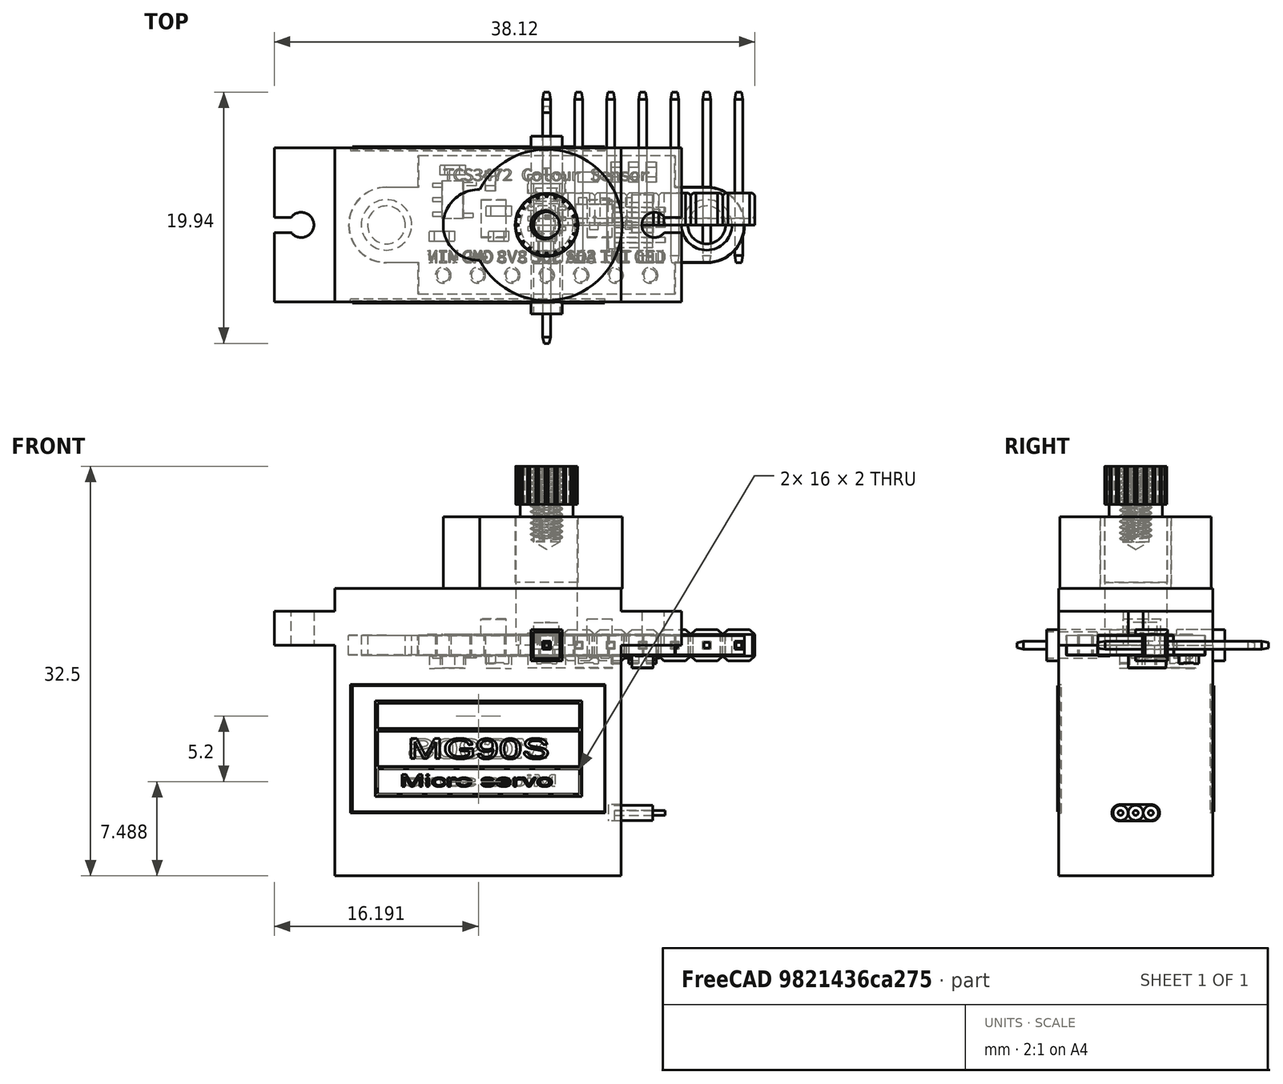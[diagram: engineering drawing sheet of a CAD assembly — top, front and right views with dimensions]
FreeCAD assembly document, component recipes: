
FREECAD ASSEMBLY — COMPONENT RECIPES ("Gems Sorter")

This assembly document has 104 components, labeled P0..P103 below (a component is one placed body or linked part). 33 of them carry a construction recipe — the FreeCAD feature program that regenerates the part from scratch, quoted from this document or its linked companion documents; the rest are supplied as boundary geometry only. No exploded tour is included for this assembly.
COMPONENT P0 — recipe-attached ("038_Base", modeled in this document).
Construction recipe (the document's own serialized feature program — sketch geometry with constraints, then the solid features built on it; lengths are millimeters unless a unit is written):

FEATURE [Sketcher::SketchObject] Sketch
  ArcFitTolerance = 1e-06
  AttachmentSupport = -> [XY_Plane]
  FullyConstrained = true
  MakeInternals = false
  MapMode = 5
  expr: Constraints[1] = VarSet.tube_inner_dia
  expr: Constraints[3] = VarSet.dowel_dia + 5 mm
  sketch-geometry (2):
    g0: Circle CenterX=0 CenterY=0 CenterZ=0 NormalX=0 NormalY=0 NormalZ=1 AngleXU=0 Radius=42.45
    g1: Circle CenterX=0 CenterY=0 CenterZ=0 NormalX=0 NormalY=0 NormalZ=1 AngleXU=0 Radius=31.25
  constraints (4):
    c: Coincident(g0,g-1)
    c: Diameter(g0) = 84.9
    c: Coincident(g1,g0)
    c: Distance(g1,g0) = 11.2
FEATURE [PartDesign::Pad] Pad
  Direction = (0,0,1)
  Length = 7.5
  Length2 = 10
  Profile = -> Sketch
  ReferenceAxis = -> Sketch [N_Axis]
  Refine = true
  Suppressed = false
  Type = 0
  expr: Length = VarSet.mdf_thickness
FEATURE [PartDesign::Plane] DatumPlane001
  AttachmentOffset = pos=(0,0,7.5) rot=(0,0,1;0rad)
  AttachmentSupport = -> [XY_Plane]
  Length = 101.88
  MapMode = 5
  Placement = pos=(0,0,7.5) rot=(0,0,1;0rad)
  ResizeMode = 0
  Width = 101.88
  expr: .AttachmentOffset.Base.z = VarSet.mdf_thickness
FEATURE [Sketcher::SketchObject] Sketch011
  ArcFitTolerance = 1e-06
  AttachmentSupport = -> [DatumPlane001]
  FullyConstrained = true
  MakeInternals = false
  MapMode = 5
  Placement = pos=(0,0,7.5) rot=(0,0,1;0rad)
  expr: Constraints[17] = VarSet.tube_inner_dia / 2 - 2.5 mm - VarSet.dowel_dia / 2
  expr: Constraints[1] = VarSet.dowel_dia
  expr: Constraints[2] = VarSet.tube_inner_dia / 2 - 2.5 mm - VarSet.dowel_dia / 2
  expr: Constraints[6] = VarSet.tube_inner_dia / 2 - 2.5 mm - VarSet.dowel_dia / 2
  sketch-geometry (8):
    g0: Circle [constr] CenterX=-36.85 CenterY=0 CenterZ=0 NormalX=0 NormalY=0 NormalZ=1 AngleXU=0 Radius=3.1
    g1: Circle CenterX=-31.913 CenterY=18.425 CenterZ=0 NormalX=0 NormalY=0 NormalZ=1 AngleXU=0 Radius=3.1
    g2: Circle CenterX=-31.913 CenterY=-18.425 CenterZ=0 NormalX=0 NormalY=0 NormalZ=1 AngleXU=0 Radius=3.1
    g3: LineSegment [constr] StartX=-31.913 StartY=-18.425 StartZ=0 EndX=0 EndY=0 EndZ=0
    g4: Circle CenterX=-18.425 CenterY=31.913 CenterZ=0 NormalX=0 NormalY=0 NormalZ=1 AngleXU=0 Radius=3.1
    g5: Circle CenterX=-18.425 CenterY=-31.913 CenterZ=0 NormalX=0 NormalY=0 NormalZ=1 AngleXU=0 Radius=3.1
    g6: LineSegment [constr] StartX=-18.425 StartY=31.913 StartZ=0 EndX=0 EndY=-3.6e-15 EndZ=0
    g7: LineSegment [constr] StartX=0 StartY=0 StartZ=0 EndX=-18.425 EndY=-31.913 EndZ=0
  constraints (19):
    c: PointOnObject(g0,g-1)
    c: Diameter(g0) = 6.2
    c: Distance(g0,g-2) = 36.85
    c: Equal(g1,g2)
    c: Equal(g2,g0)
    c: Symmetric(g2,g1,g-1)
    c: Distance(g1,g-1) = 36.85
    c: Coincident(g3,g2)
    c: Coincident(g3,g-1)
    c: Angle(g-1,g3) = 0.523599
    c: Equal(g5,g4)
    c: Equal(g4,g2)
    c: Symmetric(g5,g4,g-1)
    c: Coincident(g6,g4)
    c: Coincident(g6,g3)
    c: Coincident(g7,g3)
    c: Coincident(g7,g5)
    c: Distance(g6,g6) = 36.85
    c: Angle(g6,g-1) = 1.0472
FEATURE [PartDesign::Pocket] Pocket003
  BaseFeature = -> Pad
  Direction = (0,0,-1)
  Length = 5
  Length2 = 5
  Profile = -> Sketch011
  ReferenceAxis = -> Sketch011 [N_Axis]
  Refine = true
  Suppressed = false
  Type = 1
FEATURE [PartDesign::Plane] DatumPlane004
  AttachmentOffset = pos=(0,0,42.45) rot=(0,0,1;0rad)
  AttachmentSupport = -> [XZ_Plane]
  Length = 97.9307
  MapMode = 5
  Placement = pos=(0,-42.45,9.4e-15) rot=(1,0,0;1.5708rad)
  ResizeMode = 0
  Width = 63.0307
  expr: .AttachmentOffset.Base.z = VarSet.tube_inner_dia / 2
FEATURE [Sketcher::SketchObject] Sketch024
  ArcFitTolerance = 1e-06
  AttachmentSupport = -> [DatumPlane004]
  FullyConstrained = true
  MakeInternals = false
  MapMode = 5
  Placement = pos=(0,-42.45,9.4e-15) rot=(1,0,0;1.5708rad)
  expr: Constraints[2] = VarSet.mdf_thickness / 2
  sketch-geometry (1):
    g0: Circle CenterX=0 CenterY=3.75 CenterZ=0 NormalX=0 NormalY=0 NormalZ=1 AngleXU=0 Radius=1
  constraints (3):
    c: Diameter(g0) = 2
    c: PointOnObject(g0,g-2)
    c: Distance(g0,g-1) = 3.75
FEATURE [PartDesign::Pocket] Pocket012
  BaseFeature = -> Pocket003
  Direction = (0,1,-2e-16)
  Length = 6
  Length2 = 5
  Profile = -> Sketch024
  ReferenceAxis = -> Sketch024 [N_Axis]
  Refine = true
  Suppressed = false
  Type = 0
FEATURE [PartDesign::PolarPattern] PolarPattern001
  Angle = 180
  Axis = -> Z_Axis
  BaseFeature = -> Pocket012
  Mode = 0
  Occurrences = 3
  Offset = 120
  Originals = -> [Pocket012]
  Refine = true
  Reversed = true
  Suppressed = false
  TransformMode = 0
FEATURE [PartDesign::Body] Body  label="ring_spacer"
  AllowCompound = false
  Group = -> [Sketch,Pad,DatumPlane001,Sketch011,Pocket003,DatumPlane004,Sketch024,Pocket012,PolarPattern001]
  Origin = -> Origin
  Placement = pos=(0,0,-12) rot=(0,0,1;0rad)
  Tip = -> PolarPattern001
COMPONENT P1 — same part as P0; its construction recipe is shown at P0.
COMPONENT P2 — same part as P0; its construction recipe is shown at P0.
COMPONENT P3 — geometry summary ("059_BreadBoard001"; no construction recipe available for this part):
  bounding box: 83.8 x 55.5 x 8.0 mm
  tessellated surface: 18,878 triangles
  volume: 30349 mm^3 (81% of its bounding box)
COMPONENT P4 — recipe-attached ("037_Cap", modeled in this document).
Construction recipe (the document's own serialized feature program — sketch geometry with constraints, then the solid features built on it; lengths are millimeters unless a unit is written):

FEATURE [Sketcher::SketchObject] Sketch001
  ArcFitTolerance = 1e-06
  AttachmentSupport = -> [XY_Plane001]
  FullyConstrained = true
  MakeInternals = false
  MapMode = 5
  expr: Constraints[2] = VarSet.pipe_OD
  expr: Constraints[3] = VarSet.Pipe_thickness
  sketch-geometry (2):
    g0: Circle CenterX=0 CenterY=0 CenterZ=0 NormalX=0 NormalY=0 NormalZ=1 AngleXU=0 Radius=45
    g1: Circle CenterX=0 CenterY=0 CenterZ=0 NormalX=0 NormalY=0 NormalZ=1 AngleXU=0 Radius=40
  constraints (4):
    c: Coincident(g0,g-1)
    c: Coincident(g1,g0)
    c: Diameter(g0) = 90
    c: Distance(g1,g0) = 5
FEATURE [PartDesign::Pad] Pad001
  Direction = (0,0,1)
  Length = 50
  Length2 = 10
  Profile = -> Sketch001
  ReferenceAxis = -> Sketch001 [N_Axis]
  Refine = true
  Suppressed = false
  Type = 0
FEATURE [PartDesign::Body] Body001  label="Pipe"
  AllowCompound = false
  Group = -> [Sketch001,Pad001]
  Origin = -> Origin001
  Placement = pos=(0,0,-42) rot=(0,0,1;0rad)
  Tip = -> Pad001
COMPONENT P5 — geometry summary ("032_Cut"; no construction recipe available for this part):
  bounding box: 32.7 x 16.0 x 9.6 mm
  tessellated surface: 1,810 triangles
  volume: 2244 mm^3 (45% of its bounding box)
COMPONENT P6 — geometry summary ("016_M90S_ali001"; no construction recipe available for this part):
  bounding box: 32.5 x 32.3 x 12.4 mm
  tessellated surface: 12,672 triangles
  volume: 7441 mm^3 (57% of its bounding box)
  symmetry: mirror-symmetric across its x mid-plane
COMPONENT P7 — geometry summary ("029_M90S_ali002"; no construction recipe available for this part):
  bounding box: 32.5 x 32.3 x 12.4 mm
  tessellated surface: 12,672 triangles
  volume: 7441 mm^3 (57% of its bounding box)
  symmetry: mirror-symmetric across its x mid-plane
COMPONENT P8 — geometry summary ("061_Pin001"; no construction recipe available for this part):
  bounding box: 18.8 x 0.6 x 0.6 mm
  tessellated surface: 28 triangles
  volume: 8 mm^3 (98% of its bounding box)
  symmetry: 2-fold rotationally symmetric about the x axis; 2-fold rotationally symmetric about the y axis; 4-fold rotationally symmetric about the z axis; mirror-symmetric across its x mid-plane, y mid-plane, z mid-plane
COMPONENT P9 — geometry summary ("064_Pin002"; no construction recipe available for this part):
  bounding box: 18.8 x 0.6 x 0.6 mm
  tessellated surface: 28 triangles
  volume: 8 mm^3 (98% of its bounding box)
  symmetry: 2-fold rotationally symmetric about the x axis; 2-fold rotationally symmetric about the y axis; 4-fold rotationally symmetric about the z axis; mirror-symmetric across its x mid-plane, y mid-plane, z mid-plane
COMPONENT P10 — geometry summary ("066_Pin003"; no construction recipe available for this part):
  bounding box: 18.8 x 0.6 x 0.6 mm
  tessellated surface: 28 triangles
  volume: 8 mm^3 (98% of its bounding box)
  symmetry: 2-fold rotationally symmetric about the x axis; 2-fold rotationally symmetric about the y axis; 4-fold rotationally symmetric about the z axis; mirror-symmetric across its x mid-plane, y mid-plane, z mid-plane
COMPONENT P11 — geometry summary ("068_Pin004"; no construction recipe available for this part):
  bounding box: 18.8 x 0.6 x 0.6 mm
  tessellated surface: 28 triangles
  volume: 8 mm^3 (98% of its bounding box)
  symmetry: 2-fold rotationally symmetric about the x axis; 2-fold rotationally symmetric about the y axis; 4-fold rotationally symmetric about the z axis; mirror-symmetric across its x mid-plane, y mid-plane, z mid-plane
COMPONENT P12 — geometry summary ("069_Pin005"; no construction recipe available for this part):
  bounding box: 18.8 x 0.6 x 0.6 mm
  tessellated surface: 28 triangles
  volume: 8 mm^3 (98% of its bounding box)
  symmetry: 2-fold rotationally symmetric about the x axis; 2-fold rotationally symmetric about the y axis; 4-fold rotationally symmetric about the z axis; mirror-symmetric across its x mid-plane, y mid-plane, z mid-plane
COMPONENT P13 — geometry summary ("071_Pin006"; no construction recipe available for this part):
  bounding box: 18.8 x 0.6 x 0.6 mm
  tessellated surface: 28 triangles
  volume: 8 mm^3 (98% of its bounding box)
  symmetry: 2-fold rotationally symmetric about the x axis; 2-fold rotationally symmetric about the y axis; 4-fold rotationally symmetric about the z axis; mirror-symmetric across its x mid-plane, y mid-plane, z mid-plane
COMPONENT P14 — geometry summary ("073_Pin007"; no construction recipe available for this part):
  bounding box: 18.8 x 0.6 x 0.6 mm
  tessellated surface: 28 triangles
  volume: 8 mm^3 (98% of its bounding box)
  symmetry: 2-fold rotationally symmetric about the x axis; 2-fold rotationally symmetric about the y axis; 4-fold rotationally symmetric about the z axis; mirror-symmetric across its x mid-plane, y mid-plane, z mid-plane
COMPONENT P15 — geometry summary ("075_Pin008"; no construction recipe available for this part):
  bounding box: 18.8 x 0.6 x 0.6 mm
  tessellated surface: 28 triangles
  volume: 8 mm^3 (98% of its bounding box)
  symmetry: 2-fold rotationally symmetric about the x axis; 2-fold rotationally symmetric about the y axis; 4-fold rotationally symmetric about the z axis; mirror-symmetric across its x mid-plane, y mid-plane, z mid-plane
COMPONENT P16 — geometry summary ("077_Pin009"; no construction recipe available for this part):
  bounding box: 18.8 x 0.6 x 0.6 mm
  tessellated surface: 28 triangles
  volume: 8 mm^3 (98% of its bounding box)
  symmetry: 2-fold rotationally symmetric about the x axis; 2-fold rotationally symmetric about the y axis; 4-fold rotationally symmetric about the z axis; mirror-symmetric across its x mid-plane, y mid-plane, z mid-plane
COMPONENT P17 — geometry summary ("079_Pin010"; no construction recipe available for this part):
  bounding box: 18.8 x 0.6 x 0.6 mm
  tessellated surface: 28 triangles
  volume: 8 mm^3 (98% of its bounding box)
  symmetry: 2-fold rotationally symmetric about the x axis; 2-fold rotationally symmetric about the y axis; 4-fold rotationally symmetric about the z axis; mirror-symmetric across its x mid-plane, y mid-plane, z mid-plane
COMPONENT P18 — geometry summary ("081_Pin011"; no construction recipe available for this part):
  bounding box: 18.8 x 0.6 x 0.6 mm
  tessellated surface: 28 triangles
  volume: 8 mm^3 (98% of its bounding box)
  symmetry: 2-fold rotationally symmetric about the x axis; 2-fold rotationally symmetric about the y axis; 4-fold rotationally symmetric about the z axis; mirror-symmetric across its x mid-plane, y mid-plane, z mid-plane
COMPONENT P19 — geometry summary ("083_Pin012"; no construction recipe available for this part):
  bounding box: 18.8 x 0.6 x 0.6 mm
  tessellated surface: 28 triangles
  volume: 8 mm^3 (98% of its bounding box)
  symmetry: 2-fold rotationally symmetric about the x axis; 2-fold rotationally symmetric about the y axis; 4-fold rotationally symmetric about the z axis; mirror-symmetric across its x mid-plane, y mid-plane, z mid-plane
COMPONENT P20 — geometry summary ("085_Pin013"; no construction recipe available for this part):
  bounding box: 18.8 x 0.6 x 0.6 mm
  tessellated surface: 28 triangles
  volume: 8 mm^3 (98% of its bounding box)
  symmetry: 2-fold rotationally symmetric about the x axis; 2-fold rotationally symmetric about the y axis; 4-fold rotationally symmetric about the z axis; mirror-symmetric across its x mid-plane, y mid-plane, z mid-plane
COMPONENT P21 — geometry summary ("087_Pin014"; no construction recipe available for this part):
  bounding box: 18.8 x 0.6 x 0.6 mm
  tessellated surface: 28 triangles
  volume: 8 mm^3 (98% of its bounding box)
  symmetry: 2-fold rotationally symmetric about the x axis; 2-fold rotationally symmetric about the y axis; 4-fold rotationally symmetric about the z axis; mirror-symmetric across its x mid-plane, y mid-plane, z mid-plane
COMPONENT P22 — geometry summary ("089_Pin015"; no construction recipe available for this part):
  bounding box: 18.8 x 0.6 x 0.6 mm
  tessellated surface: 28 triangles
  volume: 8 mm^3 (98% of its bounding box)
  symmetry: 2-fold rotationally symmetric about the x axis; 2-fold rotationally symmetric about the y axis; 4-fold rotationally symmetric about the z axis; mirror-symmetric across its x mid-plane, y mid-plane, z mid-plane
COMPONENT P23 — geometry summary ("091_Pin016"; no construction recipe available for this part):
  bounding box: 18.8 x 0.6 x 0.6 mm
  tessellated surface: 28 triangles
  volume: 8 mm^3 (98% of its bounding box)
  symmetry: 2-fold rotationally symmetric about the x axis; 2-fold rotationally symmetric about the y axis; 4-fold rotationally symmetric about the z axis; mirror-symmetric across its x mid-plane, y mid-plane, z mid-plane
COMPONENT P24 — geometry summary ("093_Pin017"; no construction recipe available for this part):
  bounding box: 18.8 x 0.6 x 0.6 mm
  tessellated surface: 28 triangles
  volume: 8 mm^3 (98% of its bounding box)
  symmetry: 2-fold rotationally symmetric about the x axis; 2-fold rotationally symmetric about the y axis; 4-fold rotationally symmetric about the z axis; mirror-symmetric across its x mid-plane, y mid-plane, z mid-plane
COMPONENT P25 — geometry summary ("095_Pin018"; no construction recipe available for this part):
  bounding box: 18.8 x 0.6 x 0.6 mm
  tessellated surface: 28 triangles
  volume: 8 mm^3 (98% of its bounding box)
  symmetry: 2-fold rotationally symmetric about the x axis; 2-fold rotationally symmetric about the y axis; 4-fold rotationally symmetric about the z axis; mirror-symmetric across its x mid-plane, y mid-plane, z mid-plane
COMPONENT P26 — geometry summary ("097_Pin019"; no construction recipe available for this part):
  bounding box: 18.8 x 0.6 x 0.6 mm
  tessellated surface: 28 triangles
  volume: 8 mm^3 (98% of its bounding box)
  symmetry: 2-fold rotationally symmetric about the x axis; 2-fold rotationally symmetric about the y axis; 4-fold rotationally symmetric about the z axis; mirror-symmetric across its x mid-plane, y mid-plane, z mid-plane
COMPONENT P27 — geometry summary ("099_Pin020"; no construction recipe available for this part):
  bounding box: 18.8 x 0.6 x 0.6 mm
  tessellated surface: 28 triangles
  volume: 8 mm^3 (98% of its bounding box)
  symmetry: 2-fold rotationally symmetric about the x axis; 2-fold rotationally symmetric about the y axis; 4-fold rotationally symmetric about the z axis; mirror-symmetric across its x mid-plane, y mid-plane, z mid-plane
COMPONENT P28 — geometry summary ("050_Socket001"; no construction recipe available for this part):
  bounding box: 14.1 x 2.5 x 2.5 mm
  tessellated surface: 220 triangles
  volume: 52 mm^3 (59% of its bounding box)
  symmetry: mirror-symmetric across its y mid-plane
COMPONENT P29 — geometry summary ("051_Socket002"; no construction recipe available for this part):
  bounding box: 14.1 x 2.5 x 2.5 mm
  tessellated surface: 220 triangles
  volume: 52 mm^3 (59% of its bounding box)
  symmetry: mirror-symmetric across its y mid-plane
COMPONENT P30 — geometry summary ("052_Socket003"; no construction recipe available for this part):
  bounding box: 14.1 x 2.5 x 2.5 mm
  tessellated surface: 220 triangles
  volume: 52 mm^3 (59% of its bounding box)
  symmetry: mirror-symmetric across its y mid-plane
COMPONENT P31 — geometry summary ("056_Socket004"; no construction recipe available for this part):
  bounding box: 14.1 x 2.5 x 2.5 mm
  tessellated surface: 220 triangles
  volume: 52 mm^3 (59% of its bounding box)
  symmetry: mirror-symmetric across its y mid-plane
COMPONENT P32 — geometry summary ("057_Socket005"; no construction recipe available for this part):
  bounding box: 14.1 x 2.5 x 2.5 mm
  tessellated surface: 220 triangles
  volume: 52 mm^3 (59% of its bounding box)
  symmetry: mirror-symmetric across its y mid-plane
COMPONENT P33 — geometry summary ("058_Socket006"; no construction recipe available for this part):
  bounding box: 14.1 x 2.5 x 2.5 mm
  tessellated surface: 220 triangles
  volume: 52 mm^3 (59% of its bounding box)
  symmetry: mirror-symmetric across its y mid-plane
COMPONENT P34 — geometry summary ("062_Socket007"; no construction recipe available for this part):
  bounding box: 14.1 x 2.5 x 2.5 mm
  tessellated surface: 220 triangles
  volume: 52 mm^3 (59% of its bounding box)
  symmetry: mirror-symmetric across its y mid-plane
COMPONENT P35 — geometry summary ("063_Socket008"; no construction recipe available for this part):
  bounding box: 14.1 x 2.5 x 2.5 mm
  tessellated surface: 220 triangles
  volume: 52 mm^3 (59% of its bounding box)
  symmetry: mirror-symmetric across its y mid-plane
COMPONENT P36 — geometry summary ("065_Socket009"; no construction recipe available for this part):
  bounding box: 14.1 x 2.5 x 2.5 mm
  tessellated surface: 220 triangles
  volume: 52 mm^3 (59% of its bounding box)
  symmetry: mirror-symmetric across its y mid-plane
COMPONENT P37 — geometry summary ("067_Socket010"; no construction recipe available for this part):
  bounding box: 14.1 x 2.5 x 2.5 mm
  tessellated surface: 220 triangles
  volume: 52 mm^3 (59% of its bounding box)
  symmetry: mirror-symmetric across its y mid-plane
COMPONENT P38 — geometry summary ("070_Socket011"; no construction recipe available for this part):
  bounding box: 14.1 x 2.5 x 2.5 mm
  tessellated surface: 220 triangles
  volume: 52 mm^3 (59% of its bounding box)
  symmetry: mirror-symmetric across its y mid-plane
COMPONENT P39 — geometry summary ("072_Socket012"; no construction recipe available for this part):
  bounding box: 14.1 x 2.5 x 2.5 mm
  tessellated surface: 220 triangles
  volume: 52 mm^3 (59% of its bounding box)
  symmetry: mirror-symmetric across its y mid-plane
COMPONENT P40 — geometry summary ("074_Socket013"; no construction recipe available for this part):
  bounding box: 14.1 x 2.5 x 2.5 mm
  tessellated surface: 220 triangles
  volume: 52 mm^3 (59% of its bounding box)
  symmetry: mirror-symmetric across its y mid-plane
COMPONENT P41 — geometry summary ("076_Socket014"; no construction recipe available for this part):
  bounding box: 14.1 x 2.5 x 2.5 mm
  tessellated surface: 220 triangles
  volume: 52 mm^3 (59% of its bounding box)
  symmetry: mirror-symmetric across its y mid-plane
COMPONENT P42 — geometry summary ("078_Socket015"; no construction recipe available for this part):
  bounding box: 14.1 x 2.5 x 2.5 mm
  tessellated surface: 220 triangles
  volume: 52 mm^3 (59% of its bounding box)
  symmetry: mirror-symmetric across its y mid-plane
COMPONENT P43 — geometry summary ("080_Socket016"; no construction recipe available for this part):
  bounding box: 14.1 x 2.5 x 2.5 mm
  tessellated surface: 220 triangles
  volume: 52 mm^3 (59% of its bounding box)
  symmetry: mirror-symmetric across its y mid-plane
COMPONENT P44 — geometry summary ("082_Socket017"; no construction recipe available for this part):
  bounding box: 14.1 x 2.5 x 2.5 mm
  tessellated surface: 220 triangles
  volume: 52 mm^3 (59% of its bounding box)
  symmetry: mirror-symmetric across its y mid-plane
COMPONENT P45 — geometry summary ("084_Socket018"; no construction recipe available for this part):
  bounding box: 14.1 x 2.5 x 2.5 mm
  tessellated surface: 220 triangles
  volume: 52 mm^3 (59% of its bounding box)
  symmetry: mirror-symmetric across its y mid-plane
COMPONENT P46 — geometry summary ("086_Socket019"; no construction recipe available for this part):
  bounding box: 14.1 x 2.5 x 2.5 mm
  tessellated surface: 220 triangles
  volume: 52 mm^3 (59% of its bounding box)
  symmetry: mirror-symmetric across its y mid-plane
COMPONENT P47 — geometry summary ("088_Socket020"; no construction recipe available for this part):
  bounding box: 14.1 x 2.5 x 2.5 mm
  tessellated surface: 220 triangles
  volume: 52 mm^3 (59% of its bounding box)
  symmetry: mirror-symmetric across its y mid-plane
COMPONENT P48 — geometry summary ("090_Socket021"; no construction recipe available for this part):
  bounding box: 14.1 x 2.5 x 2.5 mm
  tessellated surface: 220 triangles
  volume: 52 mm^3 (59% of its bounding box)
  symmetry: mirror-symmetric across its y mid-plane
COMPONENT P49 — geometry summary ("092_Socket022"; no construction recipe available for this part):
  bounding box: 14.1 x 2.5 x 2.5 mm
  tessellated surface: 220 triangles
  volume: 52 mm^3 (59% of its bounding box)
  symmetry: mirror-symmetric across its y mid-plane
COMPONENT P50 — geometry summary ("094_Socket023"; no construction recipe available for this part):
  bounding box: 14.1 x 2.5 x 2.5 mm
  tessellated surface: 220 triangles
  volume: 52 mm^3 (59% of its bounding box)
  symmetry: mirror-symmetric across its y mid-plane
COMPONENT P51 — geometry summary ("096_Socket024"; no construction recipe available for this part):
  bounding box: 14.1 x 2.5 x 2.5 mm
  tessellated surface: 220 triangles
  volume: 52 mm^3 (59% of its bounding box)
  symmetry: mirror-symmetric across its y mid-plane
COMPONENT P52 — geometry summary ("098_Socket025"; no construction recipe available for this part):
  bounding box: 14.1 x 2.5 x 2.5 mm
  tessellated surface: 220 triangles
  volume: 52 mm^3 (59% of its bounding box)
  symmetry: mirror-symmetric across its y mid-plane
COMPONENT P53 — geometry summary ("100_Socket026"; no construction recipe available for this part):
  bounding box: 14.1 x 2.5 x 2.5 mm
  tessellated surface: 220 triangles
  volume: 52 mm^3 (59% of its bounding box)
  symmetry: mirror-symmetric across its y mid-plane
COMPONENT P54 — geometry summary ("101_Socket027"; no construction recipe available for this part):
  bounding box: 14.1 x 2.5 x 2.5 mm
  tessellated surface: 220 triangles
  volume: 52 mm^3 (59% of its bounding box)
  symmetry: mirror-symmetric across its y mid-plane
COMPONENT P55 — geometry summary ("102_Socket028"; no construction recipe available for this part):
  bounding box: 14.1 x 2.5 x 2.5 mm
  tessellated surface: 220 triangles
  volume: 52 mm^3 (59% of its bounding box)
  symmetry: mirror-symmetric across its y mid-plane
COMPONENT P56 — geometry summary ("103_Socket029"; no construction recipe available for this part):
  bounding box: 14.1 x 2.5 x 2.5 mm
  tessellated surface: 220 triangles
  volume: 52 mm^3 (59% of its bounding box)
  symmetry: mirror-symmetric across its y mid-plane
COMPONENT P57 — geometry summary ("104_Socket030"; no construction recipe available for this part):
  bounding box: 14.1 x 2.5 x 2.5 mm
  tessellated surface: 220 triangles
  volume: 52 mm^3 (59% of its bounding box)
  symmetry: mirror-symmetric across its y mid-plane
COMPONENT P58 — geometry summary ("020_#2x1/4in-Screw001"; no construction recipe available for this part):
  bounding box: 6.3 x 4.1 x 4.1 mm
  tessellated surface: 3,434 triangles
  volume: 23 mm^3 (22% of its bounding box)
  symmetry: 4-fold rotationally symmetric about the z axis; mirror-symmetric across its y mid-plane
COMPONENT P59 — geometry summary ("021_#2x1/4in-Screw002"; no construction recipe available for this part):
  bounding box: 6.3 x 4.1 x 4.1 mm
  tessellated surface: 3,434 triangles
  volume: 23 mm^3 (22% of its bounding box)
  symmetry: 4-fold rotationally symmetric about the z axis; mirror-symmetric across its y mid-plane
COMPONENT P60 — geometry summary ("030_#2x1/4in-Screw003"; no construction recipe available for this part):
  bounding box: 6.3 x 4.1 x 4.1 mm
  tessellated surface: 3,434 triangles
  volume: 23 mm^3 (22% of its bounding box)
  symmetry: 4-fold rotationally symmetric about the z axis; mirror-symmetric across its y mid-plane
COMPONENT P61 — geometry summary ("031_#2x1/4in-Screw004"; no construction recipe available for this part):
  bounding box: 6.3 x 4.1 x 4.1 mm
  tessellated surface: 3,434 triangles
  volume: 23 mm^3 (22% of its bounding box)
  symmetry: 4-fold rotationally symmetric about the z axis; mirror-symmetric across its y mid-plane
COMPONENT P62 — geometry summary ("003_#3x3/8in-Screw001"; no construction recipe available for this part):
  bounding box: 9.5 x 4.5 x 4.5 mm
  tessellated surface: 2,432 triangles
  volume: 52 mm^3 (27% of its bounding box)
  symmetry: 2-fold rotationally symmetric about the y axis; mirror-symmetric across its x mid-plane, z mid-plane
COMPONENT P63 — geometry summary ("004_#3x3/8in-Screw002"; no construction recipe available for this part):
  bounding box: 9.5 x 4.5 x 4.5 mm
  tessellated surface: 2,432 triangles
  volume: 52 mm^3 (27% of its bounding box)
  symmetry: 2-fold rotationally symmetric about the y axis; mirror-symmetric across its x mid-plane, z mid-plane
COMPONENT P64 — geometry summary ("005_#3x3/8in-Screw003"; no construction recipe available for this part):
  bounding box: 9.5 x 4.5 x 4.5 mm
  tessellated surface: 2,432 triangles
  volume: 52 mm^3 (27% of its bounding box)
  symmetry: 2-fold rotationally symmetric about the y axis; mirror-symmetric across its x mid-plane, z mid-plane
COMPONENT P65 — geometry summary ("010_#3x3/8in-Screw004"; no construction recipe available for this part):
  bounding box: 9.5 x 4.5 x 4.5 mm
  tessellated surface: 2,432 triangles
  volume: 52 mm^3 (27% of its bounding box)
  symmetry: 2-fold rotationally symmetric about the y axis; mirror-symmetric across its x mid-plane, z mid-plane
COMPONENT P66 — geometry summary ("011_#3x3/8in-Screw005"; no construction recipe available for this part):
  bounding box: 9.5 x 4.5 x 4.5 mm
  tessellated surface: 2,432 triangles
  volume: 52 mm^3 (27% of its bounding box)
  symmetry: 2-fold rotationally symmetric about the y axis; mirror-symmetric across its x mid-plane, z mid-plane
COMPONENT P67 — geometry summary ("012_#3x3/8in-Screw006"; no construction recipe available for this part):
  bounding box: 9.5 x 4.5 x 4.5 mm
  tessellated surface: 2,432 triangles
  volume: 52 mm^3 (27% of its bounding box)
  symmetry: 2-fold rotationally symmetric about the y axis; mirror-symmetric across its x mid-plane, z mid-plane
COMPONENT P68 — geometry summary ("013_#3x3/8in-Screw007"; no construction recipe available for this part):
  bounding box: 9.5 x 4.5 x 4.5 mm
  tessellated surface: 2,432 triangles
  volume: 52 mm^3 (27% of its bounding box)
  symmetry: 2-fold rotationally symmetric about the y axis; mirror-symmetric across its x mid-plane, z mid-plane
COMPONENT P69 — geometry summary ("018_#3x3/8in-Screw008"; no construction recipe available for this part):
  bounding box: 9.5 x 4.5 x 4.5 mm
  tessellated surface: 2,432 triangles
  volume: 52 mm^3 (27% of its bounding box)
  symmetry: 2-fold rotationally symmetric about the y axis; mirror-symmetric across its x mid-plane, z mid-plane
COMPONENT P70 — geometry summary ("019_#3x3/8in-Screw009"; no construction recipe available for this part):
  bounding box: 9.5 x 4.5 x 4.5 mm
  tessellated surface: 2,432 triangles
  volume: 52 mm^3 (27% of its bounding box)
  symmetry: 2-fold rotationally symmetric about the y axis; mirror-symmetric across its x mid-plane, z mid-plane
COMPONENT P71 — geometry summary ("060_+++ ESP8266 NodeMCU Board +++001"; no construction recipe available for this part):
  bounding box: 48.5 x 25.7 x 12.4 mm
  tessellated surface: 45,128 triangles
  volume: 3253 mm^3 (21% of its bounding box)
COMPONENT P72 — recipe-attached ("034_3m-foam001", modeled in this document).
Construction recipe (the document's own serialized feature program — sketch geometry with constraints, then the solid features built on it; lengths are millimeters unless a unit is written):

FEATURE [Sketcher::SketchObject] Sketch027
  ArcFitTolerance = 1e-06
  AttachmentSupport = -> [XY_Plane018]
  FullyConstrained = true
  MakeInternals = false
  MapMode = 5
  sketch-geometry (5):
    g0: LineSegment StartX=-5 StartY=-7.5 StartZ=0 EndX=5 EndY=-7.5 EndZ=0
    g1: LineSegment StartX=5 StartY=-7.5 StartZ=0 EndX=5 EndY=7.5 EndZ=0
    g2: LineSegment StartX=5 StartY=7.5 StartZ=0 EndX=-5 EndY=7.5 EndZ=0
    g3: LineSegment StartX=-5 StartY=7.5 StartZ=0 EndX=-5 EndY=-7.5 EndZ=0
    g4: GeomPoint [constr] X=0 Y=0 Z=0
  constraints (12):
    c: Coincident(g0,g1)
    c: Coincident(g1,g2)
    c: Coincident(g2,g3)
    c: Coincident(g3,g0)
    c: Horizontal(g0)
    c: Horizontal(g2)
    c: Vertical(g1)
    c: Vertical(g3)
    c: Symmetric(g2,g0,g4)
    c: Distance(g1,g3) = 10
    c: Distance(g0,g2) = 15
    c: Coincident(g4,g-1)
FEATURE [PartDesign::Pad] Pad011
  Direction = (0,0,1)
  Length = 1
  Length2 = 10
  Profile = -> Sketch027
  ReferenceAxis = -> Sketch027 [N_Axis]
  Refine = true
  Suppressed = false
  Type = 0
FEATURE [PartDesign::Body] Body012  label="3m-foam"
  AllowCompound = false
  Group = -> [Sketch027,Pad011]
  Origin = -> Origin018
  Tip = -> Pad011
COMPONENT P73 — same part as P72; its construction recipe is shown at P72.
COMPONENT P74 — recipe-attached ("033_3m-sticker001", modeled in this document).
Construction recipe (the document's own serialized feature program — sketch geometry with constraints, then the solid features built on it; lengths are millimeters unless a unit is written):

FEATURE [Sketcher::SketchObject] Sketch028
  ArcFitTolerance = 1e-06
  AttachmentSupport = -> [XY_Plane019]
  FullyConstrained = true
  MakeInternals = false
  MapMode = 5
  sketch-geometry (5):
    g0: LineSegment StartX=-5 StartY=-7.5 StartZ=0 EndX=5 EndY=-7.5 EndZ=0
    g1: LineSegment StartX=5 StartY=-7.5 StartZ=0 EndX=5 EndY=7.5 EndZ=0
    g2: LineSegment StartX=5 StartY=7.5 StartZ=0 EndX=-5 EndY=7.5 EndZ=0
    g3: LineSegment StartX=-5 StartY=7.5 StartZ=0 EndX=-5 EndY=-7.5 EndZ=0
    g4: GeomPoint [constr] X=0 Y=0 Z=0
  constraints (12):
    c: Coincident(g0,g1)
    c: Coincident(g1,g2)
    c: Coincident(g2,g3)
    c: Coincident(g3,g0)
    c: Horizontal(g0)
    c: Horizontal(g2)
    c: Vertical(g1)
    c: Vertical(g3)
    c: Symmetric(g2,g0,g4)
    c: Distance(g1,g3) = 10
    c: Distance(g0,g2) = 15
    c: Coincident(g4,g-1)
FEATURE [PartDesign::Pad] Pad012
  Direction = (0,0,1)
  Length = 0.2
  Length2 = 10
  Profile = -> Sketch028
  ReferenceAxis = -> Sketch028 [N_Axis]
  Refine = true
  Suppressed = false
  Type = 0
FEATURE [PartDesign::Body] Body013  label="3m-sticker"
  AllowCompound = false
  Group = -> [Sketch028,Pad012]
  Origin = -> Origin019
  Tip = -> Pad012
COMPONENT P75 — same part as P74; its construction recipe is shown at P74.
COMPONENT P76 — geometry summary ("009_1x7 Male Pin Header009"; no construction recipe available for this part):
  bounding box: 17.8 x 13.5 x 2.5 mm
  tessellated surface: 880 triangles
  volume: 122 mm^3 (20% of its bounding box)
  symmetry: mirror-symmetric across its y mid-plane, z mid-plane
COMPONENT P77 — geometry summary ("008_color-sensor001"; no construction recipe available for this part):
  bounding box: 31.4 x 11.0 x 3.9 mm
  tessellated surface: 11,788 triangles
  volume: 473 mm^3 (35% of its bounding box)
COMPONENT P78 — recipe-attached ("007_color_sensor_layer001", modeled in this document).
Construction recipe (the document's own serialized feature program — sketch geometry with constraints, then the solid features built on it; lengths are millimeters unless a unit is written):

FEATURE [Sketcher::SketchObject] Sketch007
  ArcFitTolerance = 1e-06
  AttachmentSupport = -> [XY_Plane005]
  FullyConstrained = true
  MakeInternals = false
  MapMode = 5
  expr: Constraints[10] = VarSet.gem_hole_offset
  expr: Constraints[5] = VarSet.gem_hole_dia / 2
  expr: Constraints[8] = VarSet.tube_inner_dia / 2
  sketch-geometry (5):
    g0: LineSegment StartX=-33.0518 StartY=-26.638 StartZ=0 EndX=-4 EndY=-26.638 EndZ=0
    g1: LineSegment StartX=33.0518 StartY=-26.638 StartZ=0 EndX=4 EndY=-26.638 EndZ=0
    g2: ArcOfCircle CenterX=1.9e-15 CenterY=-20 CenterZ=0 NormalX=0 NormalY=0 NormalZ=1 AngleXU=0 Radius=7.75 StartAngle=5.25471 EndAngle=10.4532
    g3: ArcOfCircle CenterX=0 CenterY=0 CenterZ=0 NormalX=0 NormalY=0 NormalZ=1 AngleXU=0 Radius=42.45 StartAngle=5.60483 EndAngle=10.1031
    g4: Circle CenterX=0 CenterY=0 CenterZ=0 NormalX=0 NormalY=0 NormalZ=1 AngleXU=0 Radius=9
  constraints (14):
    c: Horizontal(g0)
    c: Horizontal(g1)
    c: Symmetric(g0,g1,g-2)
    c: Coincident(g2,g0)
    c: Coincident(g2,g1)
    c: Radius(g2) = 7.75
    c: Coincident(g3,g-1)
    c: Coincident(g3,g1)
    c: Radius(g3) = 42.45
    c: Coincident(g0,g3)
    c: Distance(g2,g-1) = 20
    c: DistanceX(g0,g1) = 8
    c: Coincident(g4,g3)
    c: Diameter(g4) = 18
FEATURE [PartDesign::Pad] Pad005
  Direction = (0,0,1)
  Length = 17.5
  Length2 = 10
  Profile = -> Sketch007
  ReferenceAxis = -> Sketch007 [N_Axis]
  Refine = true
  Suppressed = false
  Type = 0
  expr: Length = VarSet.mdf_thick
FEATURE [PartDesign::Fillet] Fillet
  Base = -> Pad005 [Edge5,Edge8,Edge2,Edge1]
  BaseFeature = -> Pad005
  Radius = 1.5
  Refine = true
  SupportTransform = false
  Suppressed = false
  UseAllEdges = false
  expr: Radius = VarSet.fillet_radius
FEATURE [PartDesign::Plane] DatumPlane002
  AttachmentOffset = pos=(0,0,42.45) rot=(0,0,1;0rad)
  AttachmentSupport = -> [YZ_Plane005]
  Length = 80.8428
  MapMode = 5
  Placement = pos=(42.45,0,0) rot=(0.57735,0.57735,0.57735;2.0944rad)
  ResizeMode = 0
  Width = 61.7548
  expr: .AttachmentOffset.Base.z = VarSet.tube_inner_dia / 2
FEATURE [Sketcher::SketchObject] Sketch022
  ArcFitTolerance = 1e-06
  AttachmentSupport = -> [DatumPlane002]
  FullyConstrained = true
  MakeInternals = false
  MapMode = 5
  Placement = pos=(42.45,0,0) rot=(0.57735,0.57735,0.57735;2.0944rad)
  expr: Constraints[2] = VarSet.mdf_thick / 2
  sketch-geometry (1):
    g0: Circle CenterX=0 CenterY=8.75 CenterZ=0 NormalX=0 NormalY=0 NormalZ=1 AngleXU=0 Radius=1.5
  constraints (3):
    c: PointOnObject(g0,g-2)
    c: Diameter(g0) = 3
    c: DistanceY(g-1,g0) = 8.75
FEATURE [PartDesign::Pocket] Pocket010
  BaseFeature = -> Fillet
  Direction = (-1,0,0)
  Length = 5
  Length2 = 5
  Profile = -> Sketch022
  ReferenceAxis = -> Sketch022 [N_Axis]
  Refine = true
  Suppressed = false
  Type = 0
FEATURE [PartDesign::Plane] DatumPlane003
  AttachmentOffset = pos=(0,0,26.7) rot=(0,0,1;0rad)
  AttachmentSupport = -> [XZ_Plane005]
  Length = 97.9307
  MapMode = 5
  Placement = pos=(0,-26.7,5.9e-15) rot=(1,0,0;1.5708rad)
  ResizeMode = 0
  Width = 63.0307
FEATURE [Sketcher::SketchObject] Sketch023
  ArcFitTolerance = 1e-06
  AttachmentSupport = -> [DatumPlane003]
  FullyConstrained = true
  MakeInternals = false
  MapMode = 5
  Placement = pos=(0,-26.7,5.9e-15) rot=(1,0,0;1.5708rad)
  sketch-geometry (2):
    g0: Circle CenterX=12.5 CenterY=6 CenterZ=0 NormalX=0 NormalY=0 NormalZ=1 AngleXU=0 Radius=0.75
    g1: Circle CenterX=-12.5 CenterY=6 CenterZ=0 NormalX=0 NormalY=0 NormalZ=1 AngleXU=0 Radius=0.75
  constraints (5):
    c: Diameter(g0) = 1.5
    c: Equal(g1,g0)
    c: Symmetric(g1,g0,g-2)
    c: DistanceX(g1,g0) = 25
    c: Distance(g1,g-1) = 6
FEATURE [PartDesign::Pocket] Pocket011
  BaseFeature = -> Pocket010
  Direction = (0,1,-2e-16)
  Length = 10
  Length2 = 5
  Profile = -> Sketch023
  ReferenceAxis = -> Sketch023 [N_Axis]
  Refine = true
  Suppressed = false
  Type = 0
FEATURE [PartDesign::Plane] DatumPlane006
  AttachmentOffset = pos=(0,0,-42.45) rot=(0,0,1;0rad)
  AttachmentSupport = -> [YZ_Plane005]
  Length = 80.8428
  MapMode = 5
  Placement = pos=(-42.45,0,0) rot=(0.57735,0.57735,0.57735;2.0944rad)
  ResizeMode = 0
  Width = 61.7548
FEATURE [Sketcher::SketchObject] Sketch026
  ArcFitTolerance = 1e-06
  AttachmentSupport = -> [DatumPlane006]
  FullyConstrained = true
  MakeInternals = false
  MapMode = 5
  Placement = pos=(-42.45,0,0) rot=(0.57735,0.57735,0.57735;2.0944rad)
  expr: Constraints[2] = VarSet.mdf_thick / 2
  sketch-geometry (1):
    g0: Circle CenterX=0 CenterY=8.75 CenterZ=0 NormalX=0 NormalY=0 NormalZ=1 AngleXU=0 Radius=1.5
  constraints (3):
    c: PointOnObject(g0,g-2)
    c: Diameter(g0) = 3
    c: Distance(g0,g-1) = 8.75
FEATURE [PartDesign::Pocket] Pocket014
  BaseFeature = -> Pocket011
  Direction = (-1,0,0)
  Length = 5
  Length2 = 5
  Profile = -> Sketch026
  ReferenceAxis = -> Sketch026 [N_Axis]
  Refine = true
  Reversed = true
  Suppressed = false
  Type = 0
FEATURE [PartDesign::Body] Body005  label="color_sensor_layer"
  AllowCompound = false
  Group = -> [Sketch007,Pad005,Fillet,DatumPlane002,Sketch022,Pocket010,DatumPlane003,Sketch023,Pocket011,DatumPlane006,Sketch026,Pocket014]
  Origin = -> Origin005
  Placement = pos=(0,0,8) rot=(0,0,1;0rad)
  Tip = -> Pocket014
COMPONENT P79 — recipe-attached ("022_dowel001", modeled in this document).
Construction recipe (the document's own serialized feature program — sketch geometry with constraints, then the solid features built on it; lengths are millimeters unless a unit is written):

FEATURE [Sketcher::SketchObject] Sketch014
  ArcFitTolerance = 1e-06
  AttachmentSupport = -> [XY_Plane008]
  FullyConstrained = true
  MakeInternals = false
  MapMode = 5
  expr: Constraints[1] = VarSet.dowel_dia - 0.05 mm
  sketch-geometry (1):
    g0: Circle CenterX=0 CenterY=0 CenterZ=0 NormalX=0 NormalY=0 NormalZ=1 AngleXU=0 Radius=3.075
  constraints (2):
    c: Coincident(g0,g-1)
    c: Diameter(g0) = 6.15
FEATURE [PartDesign::Pad] Pad008
  Direction = (0,0,1)
  Length = 71
  Length2 = 10
  Profile = -> Sketch014
  ReferenceAxis = -> Sketch014 [N_Axis]
  Refine = true
  Suppressed = false
  Type = 0
FEATURE [PartDesign::Body] Body008  label="dowel"
  AllowCompound = false
  Group = -> [Sketch014,Pad008]
  Origin = -> Origin008
  Tip = -> Pad008
COMPONENT P80 — same part as P79; its construction recipe is shown at P79.
COMPONENT P81 — same part as P79; its construction recipe is shown at P79.
COMPONENT P82 — same part as P79; its construction recipe is shown at P79.
COMPONENT P83 — recipe-attached ("014_first_layer001", modeled in this document).
Construction recipe (the document's own serialized feature program — sketch geometry with constraints, then the solid features built on it; lengths are millimeters unless a unit is written):

FEATURE [Sketcher::SketchObject] Sketch006
  ArcFitTolerance = 1e-06
  AttachmentSupport = -> [XY_Plane004]
  FullyConstrained = true
  MakeInternals = false
  MapMode = 5
  expr: Constraints[21] = VarSet.fillet_radius
  expr: Constraints[29] = VarSet.shaft_width
  expr: Constraints[2] = VarSet.gem_hole_dia - 1 mm
  expr: Constraints[3] = VarSet.gem_hole_offset
  expr: Constraints[4] = VarSet.tube_inner_dia - VarSet.rotation_tolerence
  sketch-geometry (13):
    g0: Circle CenterX=0 CenterY=0 CenterZ=0 NormalX=0 NormalY=0 NormalZ=1 AngleXU=0 Radius=41.2
    g1: Circle CenterX=0 CenterY=-20 CenterZ=0 NormalX=0 NormalY=0 NormalZ=1 AngleXU=0 Radius=7.25
    g2: GeomPoint [constr] X=0 Y=0 Z=0
    g3: LineSegment StartX=-7.42462 StartY=-1.06066 StartZ=0 EndX=-1.06066 EndY=-7.42462 EndZ=0
    g4: LineSegment StartX=1.06066 StartY=-7.42462 StartZ=0 EndX=7.42462 EndY=-1.06066 EndZ=0
    g5: LineSegment StartX=7.42462 StartY=1.06066 StartZ=0 EndX=1.06066 EndY=7.42462 EndZ=0
    g6: LineSegment StartX=-1.06066 StartY=7.42462 StartZ=0 EndX=-7.42462 EndY=1.06066 EndZ=0
    g7: ArcOfCircle CenterX=-6.36396 CenterY=0 CenterZ=0 NormalX=0 NormalY=0 NormalZ=1 AngleXU=0 Radius=1.5 StartAngle=2.35619 EndAngle=3.92699
    g8: ArcOfCircle CenterX=0 CenterY=-6.36396 CenterZ=0 NormalX=0 NormalY=0 NormalZ=1 AngleXU=0 Radius=1.5 StartAngle=3.92699 EndAngle=5.49779
    g9: ArcOfCircle CenterX=6.36396 CenterY=1.5e-15 CenterZ=0 NormalX=0 NormalY=0 NormalZ=1 AngleXU=0 Radius=1.5 StartAngle=5.49779 EndAngle=7.06858
    g10: ArcOfCircle CenterX=0 CenterY=6.36396 CenterZ=0 NormalX=0 NormalY=0 NormalZ=1 AngleXU=0 Radius=1.5 StartAngle=0.785398 EndAngle=2.35619
    g11: GeomPoint [constr] X=-8.48528 Y=-5e-16 Z=0
    g12: GeomPoint [constr] X=8.48528 Y=1.3e-15 Z=0
  constraints (30):
    c: Coincident(g0,g-1)
    c: PointOnObject(g1,g-2)
    c: Diameter(g1) = 14.5
    c: Distance(g1,g-1) = 20
    c: Diameter(g0) = 82.4
    c: Coincident(g2,g0)
    c: Tangent(g3,g7) = -1.5708
    c: Tangent(g3,g8) = -1.5708
    c: Tangent(g4,g8) = -1.5708
    c: Tangent(g4,g9) = -1.5708
    c: Tangent(g5,g9) = -1.5708
    c: Tangent(g5,g10) = -1.5708
    c: Tangent(g6,g10) = -1.5708
    c: Tangent(g6,g7) = -1.5708
    c: Equal(g7,g8)
    c: Equal(g8,g9)
    c: Equal(g9,g10)
    c: PointOnObject(g11,g3)
    c: PointOnObject(g11,g6)
    c: PointOnObject(g12,g4)
    c: PointOnObject(g12,g5)
    c: Radius(g8) = 1.5
    c: Equal(g6,g3)
    c: PointOnObject(g10,g-2)
    c: PointOnObject(g8,g-2)
    c: Parallel(g6,g4)
    c: Parallel(g3,g5)
    c: Perpendicular(g5,g6)
    c: PointOnObject(g7,g-1)
    c: Distance(g6,g6) = 9
FEATURE [PartDesign::Pad] Pad004
  Direction = (0,0,1)
  Length = 7.5
  Length2 = 10
  Profile = -> Sketch006
  ReferenceAxis = -> Sketch006 [N_Axis]
  Refine = true
  Suppressed = false
  Type = 0
  expr: Length = VarSet.mdf_thickness
FEATURE [Sketcher::SketchObject] Sketch020
  ArcFitTolerance = 1e-06
  AttachmentSupport = -> [Pad004]
  ExternalGeometry = -> [Pad004]
  FullyConstrained = true
  MakeInternals = false
  MapMode = 5
  Placement = pos=(0,0,7.5) rot=(0,0,1;0rad)
  sketch-geometry (4):
    g0: LineSegment StartX=22.396 StartY=-24.5173 StartZ=0 EndX=28.0528 EndY=-30.1741 EndZ=0
    g1: LineSegment StartX=24.5173 StartY=-22.396 StartZ=0 EndX=30.1741 EndY=-28.0528 EndZ=0
    g2: LineSegment StartX=24.5173 StartY=-22.396 StartZ=0 EndX=22.396 EndY=-24.5173 EndZ=0
    g3: ArcOfCircle CenterX=0 CenterY=0 CenterZ=0 NormalX=0 NormalY=0 NormalZ=1 AngleXU=0 Radius=41.2 StartAngle=5.46137 EndAngle=5.5342
  constraints (12):
    c: Coincident(g2,g1)
    c: Coincident(g2,g0)
    c: Coincident(g3,g-1)
    c: Coincident(g3,g0)
    c: Parallel(g0,g1)
    c: Equal(g0,g1)
    c: Perpendicular(g0,g2)
    c: PointOnObject(g0,g-3)
    c: Coincident(g1,g3)
    c: Distance(g2,g2) = 3
    c: Distance(g1,g1) = 8
    c: Parallel(g2,g-4)
FEATURE [PartDesign::Pocket] Pocket009
  BaseFeature = -> Pad004
  Direction = (0,0,-1)
  Length = 2
  Length2 = 5
  Profile = -> Sketch020
  ReferenceAxis = -> Sketch020 [N_Axis]
  Refine = true
  Suppressed = false
  Type = 0
FEATURE [PartDesign::Body] Body004  label="first_layer"
  AllowCompound = false
  Group = -> [Sketch006,Pad004,Sketch020,Pocket009]
  Origin = -> Origin004
  Placement = pos=(0,0,23) rot=(0,0,1;0rad)
  Tip = -> Pocket009
COMPONENT P84 — same part as P0; its construction recipe is shown at P0.
COMPONENT P85 — recipe-attached ("006_second_layer001", modeled in this document).
Construction recipe (the document's own serialized feature program — sketch geometry with constraints, then the solid features built on it; lengths are millimeters unless a unit is written):

FEATURE [Sketcher::SketchObject] Sketch004
  ArcFitTolerance = 1e-06
  AttachmentSupport = -> [XY_Plane002]
  FullyConstrained = true
  MakeInternals = false
  MapMode = 5
  expr: Constraints[0] = VarSet.tube_inner_dia - VarSet.rotation_tolerence
  expr: Constraints[2] = VarSet.gem_hole_offset
  expr: Constraints[3] = VarSet.gem_hole_dia
  sketch-geometry (2):
    g0: Circle CenterX=0 CenterY=0 CenterZ=0 NormalX=0 NormalY=0 NormalZ=1 AngleXU=0 Radius=41.2
    g1: Circle CenterX=0 CenterY=-20 CenterZ=0 NormalX=0 NormalY=0 NormalZ=1 AngleXU=0 Radius=7.75
  constraints (5):
    c: Diameter(g0) = 82.4
    c: PointOnObject(g1,g-2)
    c: Distance(g1,g-1) = 20
    c: Diameter(g1) = 15.5
    c: Coincident(g-1,g0)
FEATURE [PartDesign::Pad] Pad002
  Direction = (0,0,1)
  Length = 7.5
  Length2 = 10
  Profile = -> Sketch004
  ReferenceAxis = -> Sketch004 [N_Axis]
  Refine = true
  Suppressed = false
  Type = 0
  expr: Length = VarSet.mdf_thickness
FEATURE [Sketcher::SketchObject] Sketch018
  ArcFitTolerance = 1e-06
  AttachmentSupport = -> [Pad002]
  ExternalGeometry = -> [Pad002]
  FullyConstrained = true
  MakeInternals = false
  MapMode = 5
  Placement = pos=(0,0,7.5) rot=(0,0,1;0rad)
  sketch-geometry (4):
    g0: LineSegment StartX=-1.5 StartY=-33.1727 StartZ=0 EndX=-1.5 EndY=-41.1727 EndZ=0
    g1: LineSegment StartX=1.5 StartY=-41.1727 StartZ=0 EndX=1.5 EndY=-33.1727 EndZ=0
    g2: LineSegment StartX=1.5 StartY=-33.1727 StartZ=0 EndX=-1.5 EndY=-33.1727 EndZ=0
    g3: ArcOfCircle CenterX=0 CenterY=0 CenterZ=0 NormalX=0 NormalY=0 NormalZ=1 AngleXU=0 Radius=41.2 StartAngle=4.67597 EndAngle=4.7488
  constraints (11):
    c: Coincident(g1,g2)
    c: Coincident(g2,g0)
    c: Vertical(g0)
    c: Vertical(g1)
    c: Coincident(g3,g-1)
    c: Coincident(g3,g0)
    c: Coincident(g3,g1)
    c: PointOnObject(g0,g-3)
    c: Symmetric(g0,g1,g-2)
    c: Distance(g2,g2) = 3
    c: DistanceY(g1,g1) = 8
FEATURE [PartDesign::Pocket] Pocket007
  BaseFeature = -> Pad002
  Direction = (0,0,-1)
  Length = 2
  Length2 = 5
  Profile = -> Sketch018
  ReferenceAxis = -> Sketch018 [N_Axis]
  Refine = true
  Suppressed = false
  Type = 0
FEATURE [Sketcher::SketchObject] Sketch019
  ArcFitTolerance = 1e-06
  AttachmentSupport = -> [Pocket007]
  FullyConstrained = true
  MakeInternals = false
  MapMode = 5
  Placement = pos=(0,0,7.5) rot=(0,0,1;0rad)
  sketch-geometry (12):
    g0: LineSegment StartX=-6 StartY=4.5 StartZ=0 EndX=-6 EndY=-4.5 EndZ=0
    g1: LineSegment StartX=-4.5 StartY=-6 StartZ=0 EndX=4.5 EndY=-6 EndZ=0
    g2: LineSegment StartX=6 StartY=-4.5 StartZ=0 EndX=6 EndY=4.5 EndZ=0
    g3: LineSegment StartX=4.5 StartY=6 StartZ=0 EndX=-4.5 EndY=6 EndZ=0
    g4: ArcOfCircle CenterX=-4.5 CenterY=4.5 CenterZ=0 NormalX=0 NormalY=0 NormalZ=1 AngleXU=0 Radius=1.5 StartAngle=1.5708 EndAngle=3.14159
    g5: ArcOfCircle CenterX=-4.5 CenterY=-4.5 CenterZ=0 NormalX=0 NormalY=0 NormalZ=1 AngleXU=0 Radius=1.5 StartAngle=3.14159 EndAngle=4.71239
    g6: ArcOfCircle CenterX=4.5 CenterY=-4.5 CenterZ=0 NormalX=0 NormalY=0 NormalZ=1 AngleXU=0 Radius=1.5 StartAngle=4.71239 EndAngle=6.28319
    g7: ArcOfCircle CenterX=4.5 CenterY=4.5 CenterZ=0 NormalX=0 NormalY=0 NormalZ=1 AngleXU=0 Radius=1.5 StartAngle=0 EndAngle=1.5708
    g8: GeomPoint [constr] X=-6 Y=6 Z=0
    g9: GeomPoint [constr] X=6 Y=-6 Z=0
    g10: LineSegment [constr] StartX=-4.5 StartY=4.5 StartZ=0 EndX=4.5 EndY=-4.5 EndZ=0
    g11: LineSegment [constr] StartX=4.5 StartY=4.5 StartZ=0 EndX=0 EndY=0 EndZ=0
  constraints (27):
    c: Tangent(g0,g4) = -1.5708
    c: Tangent(g0,g5) = -1.5708
    c: Tangent(g1,g5) = -1.5708
    c: Tangent(g1,g6) = -1.5708
    c: Tangent(g2,g6) = -1.5708
    c: Tangent(g2,g7) = -1.5708
    c: Tangent(g3,g7) = -1.5708
    c: Tangent(g3,g4) = -1.5708
    c: Vertical(g0)
    c: Vertical(g2)
    c: Horizontal(g1)
    c: Horizontal(g3)
    c: Equal(g4,g5)
    c: Equal(g5,g6)
    c: Equal(g6,g7)
    c: PointOnObject(g8,g0)
    c: PointOnObject(g8,g3)
    c: PointOnObject(g9,g1)
    c: PointOnObject(g9,g2)
    c: Radius(g4) = 1.5
    c: Distance(g3,g3) = 9
    c: Equal(g3,g2)
    c: Coincident(g10,g4)
    c: Coincident(g10,g6)
    c: Coincident(g11,g7)
    c: Symmetric(g10,g10,g11)
    c: Coincident(g11,g-1)
FEATURE [PartDesign::Pocket] Pocket008
  BaseFeature = -> Pocket007
  Direction = (0,0,-1)
  Length = 4
  Length2 = 5
  Profile = -> Sketch019
  ReferenceAxis = -> Sketch019 [N_Axis]
  Refine = true
  Suppressed = false
  Type = 0
FEATURE [PartDesign::Body] Body002  label="second_layer"
  AllowCompound = false
  Group = -> [Sketch004,Pad002,Sketch018,Pocket007,Sketch019,Pocket008]
  Origin = -> Origin002
  Placement = pos=(0,0,-3) rot=(0,0,1;1.5708rad)
  Tip = -> Pocket008
COMPONENT P86 — recipe-attached ("027_sevo_legs001", modeled in this document).
Construction recipe (the document's own serialized feature program — sketch geometry with constraints, then the solid features built on it; lengths are millimeters unless a unit is written):

FEATURE [Sketcher::SketchObject] Sketch012
  ArcFitTolerance = 1e-06
  AttachmentSupport = -> [XY_Plane007]
  FullyConstrained = true
  MakeInternals = false
  MapMode = 5
  expr: Constraints[19] = VarSet.mdf_thickness
  expr: Constraints[20] = VarSet.mdf_thickness
  expr: Constraints[21] = VarSet.servo_leg_height
  expr: Constraints[41] = VarSet.fillet_radius
  expr: Constraints[47] = VarSet.mdf_thickness / 2
  sketch-geometry (20):
    g0: LineSegment StartX=0 StartY=0 StartZ=0 EndX=0 EndY=7.5 EndZ=0
    g1: LineSegment StartX=0 StartY=7.5 StartZ=0 EndX=7.5 EndY=7.5 EndZ=0
    g2: LineSegment StartX=7.5 StartY=7.5 StartZ=0 EndX=7.5 EndY=12.0784 EndZ=0
    g3: LineSegment StartX=7.5 StartY=12.0784 StartZ=0 EndX=31.5 EndY=12.0784 EndZ=0
    g4: LineSegment StartX=31.5 StartY=12.0784 StartZ=0 EndX=31.5 EndY=-4.57843 EndZ=0
    g5: LineSegment StartX=31.5 StartY=-4.57843 StartZ=0 EndX=7.5 EndY=-4.57843 EndZ=0
    g6: LineSegment StartX=7.5 StartY=-4.57843 StartZ=0 EndX=7.5 EndY=0 EndZ=0
    g7: LineSegment StartX=7.5 StartY=0 StartZ=0 EndX=0 EndY=0 EndZ=0
    g8: LineSegment StartX=12.5 StartY=6.57843 StartZ=0 EndX=12.5 EndY=0.921573 EndZ=0
    g9: LineSegment StartX=14 StartY=-0.578427 StartZ=0 EndX=19.6569 EndY=-0.578427 EndZ=0
    g10: LineSegment StartX=21.1569 StartY=0.921573 StartZ=0 EndX=21.1569 EndY=6.57843 EndZ=0
    g11: LineSegment StartX=19.6569 StartY=8.07843 StartZ=0 EndX=14 EndY=8.07843 EndZ=0
    g12: ArcOfCircle CenterX=14 CenterY=6.57843 CenterZ=0 NormalX=0 NormalY=0 NormalZ=1 AngleXU=0 Radius=1.5 StartAngle=1.5708 EndAngle=3.14159
    g13: ArcOfCircle CenterX=14 CenterY=0.921573 CenterZ=0 NormalX=0 NormalY=0 NormalZ=1 AngleXU=0 Radius=1.5 StartAngle=3.14159 EndAngle=4.71239
    g14: ArcOfCircle CenterX=19.6569 CenterY=0.921573 CenterZ=0 NormalX=0 NormalY=0 NormalZ=1 AngleXU=0 Radius=1.5 StartAngle=4.71239 EndAngle=6.28319
    g15: ArcOfCircle CenterX=19.6569 CenterY=6.57843 CenterZ=0 NormalX=0 NormalY=0 NormalZ=1 AngleXU=0 Radius=1.5 StartAngle=0 EndAngle=1.5708
    g16: GeomPoint [constr] X=12.5 Y=8.07843 Z=0
    g17: GeomPoint [constr] X=21.1569 Y=-0.578427 Z=0
    g18: LineSegment [constr] StartX=14 StartY=6.57843 StartZ=0 EndX=19.6569 EndY=0.921573 EndZ=0
    g19: LineSegment [constr] StartX=14 StartY=0.921573 StartZ=0 EndX=16.8284 EndY=3.75 EndZ=0
  constraints (51):
    c: Coincident(g0,g-1)
    c: PointOnObject(g0,g-2)
    c: Coincident(g0,g1)
    c: Horizontal(g1)
    c: Coincident(g1,g2)
    c: Vertical(g2)
    c: Coincident(g2,g3)
    c: Coincident(g3,g4)
    c: Vertical(g4)
    c: Coincident(g4,g5)
    c: Horizontal(g5)
    c: Coincident(g5,g6)
    c: PointOnObject(g6,g-1)
    c: Vertical(g6)
    c: Coincident(g6,g7)
    c: Coincident(g7,g0)
    c: Equal(g1,g7)
    c: Equal(g3,g5)
    c: Equal(g2,g6)
    c: DistanceX(g1,g1) = 7.5
    c: Distance(g0,g0) = 7.5
    c: DistanceX(g5,g5) = 24
    c: Tangent(g8,g12) = -1.5708
    c: Tangent(g8,g13) = -1.5708
    c: Tangent(g9,g13) = -1.5708
    c: Tangent(g9,g14) = -1.5708
    c: Tangent(g10,g14) = -1.5708
    c: Tangent(g10,g15) = -1.5708
    c: Tangent(g11,g15) = -1.5708
    c: Tangent(g11,g12) = -1.5708
    c: Vertical(g8)
    c: Vertical(g10)
    c: Horizontal(g9)
    c: Horizontal(g11)
    c: Equal(g12,g13)
    c: Equal(g13,g14)
    c: Equal(g14,g15)
    c: PointOnObject(g16,g8)
    c: PointOnObject(g16,g11)
    c: PointOnObject(g17,g9)
    c: PointOnObject(g17,g10)
    c: Radius(g13) = 1.5
    c: Coincident(g18,g12)
    c: Coincident(g18,g14)
    c: Coincident(g19,g13)
    c: Symmetric(g18,g18,g19)
    c: Equal(g11,g8)
    c: Distance(g19,g-1) = 3.75
    c: Distance(g18,g18) = 8
    c: Distance(g2,g8) = 5
    c: Distance(g5,g9) = 4
FEATURE [PartDesign::Pad] Pad007
  Direction = (0,0,1)
  Length = 7.5
  Length2 = 10
  Profile = -> Sketch012
  ReferenceAxis = -> Sketch012 [N_Axis]
  Refine = true
  Suppressed = false
  Type = 0
  expr: Length = VarSet.mdf_thickness
FEATURE [Sketcher::SketchObject] Sketch015
  ArcFitTolerance = 1e-06
  AttachmentSupport = -> [Pad007]
  ExternalGeometry = -> [Pad007]
  FullyConstrained = false
  MakeInternals = false
  MapMode = 5
  Placement = pos=(31.5,0,0) rot=(0.57735,0.57735,0.57735;2.0944rad)
  sketch-geometry (1):
    g0: Circle CenterX=3.87266 CenterY=2.4 CenterZ=0 NormalX=0 NormalY=0 NormalZ=1 AngleXU=0 Radius=0.75
  constraints (2):
    c: Distance(g0,g-3) = 2.4
    c: Diameter(g0) = 1.5
FEATURE [PartDesign::Pocket] Pocket005
  BaseFeature = -> Pad007
  Direction = (-1,0,0)
  Length = 5
  Length2 = 5
  Profile = -> Sketch015
  ReferenceAxis = -> Sketch015 [N_Axis]
  Refine = true
  Suppressed = false
  Type = 0
FEATURE [PartDesign::Body] Body007  label="sevo_legs"
  AllowCompound = false
  Group = -> [Sketch012,Pad007,Sketch015,Pocket005]
  Origin = -> Origin007
  Placement = pos=(-26,-3,23) rot=(0,1,0;4.71239rad)
  Tip = -> Pocket005
COMPONENT P87 — same part as P86; its construction recipe is shown at P86.
COMPONENT P88 — geometry summary ("015_shaft001"; no construction recipe available for this part):
  bounding box: 44.0 x 11.2 x 11.2 mm
  tessellated surface: 3,672 triangles
  volume: 4099 mm^3 (74% of its bounding box)
  symmetry: 4-fold rotationally symmetric about the z axis; mirror-symmetric across its y mid-plane
COMPONENT P89 — same part as P0; its construction recipe is shown at P0.
COMPONENT P90 — same part as P0; its construction recipe is shown at P0.
COMPONENT P91 — same part as P0; its construction recipe is shown at P0.
COMPONENT P92 — same part as P0; its construction recipe is shown at P0.
COMPONENT P93 — same part as P0; its construction recipe is shown at P0.
COMPONENT P94 — same part as P0; its construction recipe is shown at P0.
COMPONENT P95 — same part as P0; its construction recipe is shown at P0.
COMPONENT P96 — recipe-attached ("026_testube_layer001", modeled in this document).
Construction recipe (the document's own serialized feature program — sketch geometry with constraints, then the solid features built on it; lengths are millimeters unless a unit is written):

FEATURE [Sketcher::SketchObject] Sketch008
  ArcFitTolerance = 1e-06
  AttachmentSupport = -> [XY_Plane006]
  FullyConstrained = false
  MakeInternals = false
  MapMode = 5
  expr: Constraints[15] = VarSet.gem_hole_offset
  expr: Constraints[16] = VarSet.gem_hole_offset + VarSet.pipe_OD / 2 + VarSet.test_tube_dia + 5 mm
  expr: Constraints[3] = VarSet.tube_inner_dia / 2
  sketch-geometry (6):
    g0: ArcOfCircle CenterX=0 CenterY=0 CenterZ=0 NormalX=0 NormalY=0 NormalZ=1 AngleXU=0 Radius=42.45 StartAngle=1.5708 EndAngle=4.71239
    g1: LineSegment [constr] StartX=2.6e-15 StartY=42.45 StartZ=0 EndX=0 EndY=85.6971 EndZ=0
    g2: LineSegment [constr] StartX=0 StartY=-42.45 StartZ=0 EndX=0 EndY=-85.6971 EndZ=0
    g3: LineSegment StartX=2.6e-15 StartY=42.45 StartZ=0 EndX=27.4414 EndY=72.9268 EndZ=0
    g4: LineSegment StartX=0 StartY=-42.45 StartZ=0 EndX=27.4414 EndY=-72.9268 EndZ=0
    g5: ArcOfCircle CenterX=-20 CenterY=0 CenterZ=0 NormalX=0 NormalY=0 NormalZ=1 AngleXU=0 Radius=87 StartAngle=5.28914 EndAngle=7.27723
  constraints (17):
    c: Coincident(g0,g-1)
    c: PointOnObject(g0,g-2)
    c: PointOnObject(g0,g-2)
    c: Radius(g0) = 42.45
    c: PointOnObject(g1,g-2)
    c: PointOnObject(g2,g-2)
    c: Coincident(g1,g0)
    c: Coincident(g2,g0)
    c: Coincident(g3,g0)
    c: Angle(g3,g1) = 0.733038
    c: Coincident(g4,g0)
    c: Angle(g2,g4) = 0.733038
    c: PointOnObject(g5,g-1)
    c: Coincident(g5,g3)
    c: Coincident(g5,g4)
    c: Distance(g5,g-2) = 20
    c: Radius(g5) = 87
FEATURE [PartDesign::Pad] Pad006
  Direction = (0,0,1)
  Length = 7.5
  Length2 = 10
  Profile = -> Sketch008
  ReferenceAxis = -> Sketch008 [N_Axis]
  Refine = true
  Suppressed = false
  Type = 0
  expr: Length = VarSet.mdf_thickness
FEATURE [PartDesign::Plane] DatumPlane
  AttachmentOffset = pos=(0,0,7.5) rot=(0,0,1;0rad)
  AttachmentSupport = -> [XY_Plane006]
  Length = 134.506
  MapMode = 5
  Placement = pos=(0,0,7.5) rot=(0,0,1;0rad)
  ResizeMode = 0
  Width = 171.101
  expr: .AttachmentOffset.Base.z = VarSet.mdf_thickness
FEATURE [Sketcher::SketchObject] Sketch009
  ArcFitTolerance = 1e-06
  AttachmentSupport = -> [DatumPlane]
  FullyConstrained = true
  MakeInternals = false
  MapMode = 5
  Placement = pos=(0,0,7.5) rot=(0,0,1;0rad)
  expr: Constraints[1] = VarSet.test_tube_dia
  expr: Constraints[2] = VarSet.pipe_OD / 2 + VarSet.test_tube_dia / 2
  sketch-geometry (1):
    g0: Circle CenterX=53.5 CenterY=0 CenterZ=0 NormalX=0 NormalY=0 NormalZ=1 AngleXU=0 Radius=8.5
  constraints (3):
    c: PointOnObject(g0,g-1)
    c: Diameter(g0) = 17
    c: Distance(g0,g-2) = 53.5
FEATURE [PartDesign::Pocket] Pocket
  BaseFeature = -> Pad006
  Direction = (0,0,-1)
  Length = 5
  Length2 = 5
  Profile = -> Sketch009
  ReferenceAxis = -> Sketch009 [N_Axis]
  Refine = true
  Suppressed = false
  Type = 1
FEATURE [PartDesign::Line] DatumLine
  AttacherType = Attacher::AttachEngineLine
  AttachmentOffset = pos=(-20,0,0) rot=(0,0,1;0rad)
  AttachmentSupport = -> [Z_Axis006]
  Length = 20
  MapMode = 29
  Placement = pos=(-20,0,0) rot=(0,0,1;0rad)
  ResizeMode = 0
  expr: .AttachmentOffset.Base.x = -VarSet.gem_hole_offset
FEATURE [PartDesign::PolarPattern] PolarPattern
  Angle = 360
  Axis = -> DatumLine
  BaseFeature = -> Pocket
  Mode = 0
  Occurrences = 22
  Offset = 120
  Originals = -> [Pocket]
  Refine = true
  Suppressed = false
  TransformMode = 0
FEATURE [Sketcher::SketchObject] Sketch010
  ArcFitTolerance = 1e-06
  AttachmentSupport = -> [DatumPlane]
  FullyConstrained = false
  MakeInternals = false
  MapMode = 5
  Placement = pos=(0,0,7.5) rot=(0,0,1;0rad)
  expr: Constraints[1] = VarSet.gem_hole_offset
  expr: Constraints[21] = VarSet.servo_length
  sketch-geometry (9):
    g0: LineSegment [constr] StartX=-20 StartY=14.1317 StartZ=0 EndX=-20 EndY=-18.2085 EndZ=0
    g1: LineSegment StartX=-34 StartY=4.05 StartZ=0 EndX=-34 EndY=-4.05 EndZ=0
    g2: LineSegment StartX=-34 StartY=-4.05 StartZ=0 EndX=-25.9 EndY=-4.05 EndZ=0
    g3: LineSegment StartX=-25.9 StartY=-4.05 StartZ=0 EndX=-25.9 EndY=4.05 EndZ=0
    g4: LineSegment StartX=-25.9 StartY=4.05 StartZ=0 EndX=-34 EndY=4.05 EndZ=0
    g5: LineSegment StartX=-2.9 StartY=4.05 StartZ=0 EndX=-2.9 EndY=-4.05 EndZ=0
    g6: LineSegment StartX=-2.9 StartY=-4.05 StartZ=0 EndX=5.2 EndY=-4.05 EndZ=0
    g7: LineSegment StartX=5.2 StartY=-4.05 StartZ=0 EndX=5.2 EndY=4.05 EndZ=0
    g8: LineSegment StartX=5.2 StartY=4.05 StartZ=0 EndX=-2.9 EndY=4.05 EndZ=0
  constraints (24):
    c: Vertical(g0)
    c: Distance(g-2,g0) = 20
    c: Coincident(g1,g2)
    c: Coincident(g2,g3)
    c: Coincident(g3,g4)
    c: Coincident(g4,g1)
    c: Vertical(g3)
    c: Horizontal(g2)
    c: Horizontal(g4)
    c: Coincident(g5,g6)
    c: Coincident(g6,g7)
    c: Coincident(g7,g8)
    c: Coincident(g8,g5)
    c: Vertical(g7)
    c: Horizontal(g6)
    c: Horizontal(g8)
    c: Equal(g4,g1)
    c: Equal(g1,g8)
    c: Equal(g8,g5)
    c: Symmetric(g1,g1,g-1)
    c: Symmetric(g5,g5,g-1)
    c: Distance(g5,g3) = 23
    c: Distance(g0,g3) = 5.9
    c: DistanceX(g4,g4) = 8.1
FEATURE [PartDesign::Pocket] Pocket001
  BaseFeature = -> PolarPattern
  Direction = (0,0,-1)
  Length = 5
  Length2 = 5
  Profile = -> Sketch010
  ReferenceAxis = -> Sketch010 [N_Axis]
  Refine = true
  Suppressed = false
  Type = 1
FEATURE [Sketcher::SketchObject] Sketch013
  ArcFitTolerance = 1e-06
  AttachmentSupport = -> [DatumPlane]
  FullyConstrained = true
  MakeInternals = false
  MapMode = 5
  Placement = pos=(0,0,7.5) rot=(0,0,1;0rad)
  expr: Constraints[5] = VarSet.tube_inner_dia / 2 - 2.5 mm - VarSet.dowel_dia / 2
  expr: Constraints[6] = VarSet.tube_inner_dia / 2 - 2.5 mm - VarSet.dowel_dia / 2
  expr: Constraints[7] = VarSet.dowel_dia
  sketch-geometry (6):
    g0: Circle CenterX=-31.913 CenterY=18.425 CenterZ=0 NormalX=0 NormalY=0 NormalZ=1 AngleXU=0 Radius=3.1
    g1: Circle CenterX=-18.425 CenterY=31.913 CenterZ=0 NormalX=0 NormalY=0 NormalZ=1 AngleXU=0 Radius=3.1
    g2: Circle CenterX=-31.913 CenterY=-18.425 CenterZ=0 NormalX=0 NormalY=0 NormalZ=1 AngleXU=0 Radius=3.1
    g3: Circle CenterX=-18.425 CenterY=-31.913 CenterZ=0 NormalX=0 NormalY=0 NormalZ=1 AngleXU=0 Radius=3.1
    g4: LineSegment [constr] StartX=-31.913 StartY=18.425 StartZ=0 EndX=0 EndY=0 EndZ=0
    g5: LineSegment [constr] StartX=-18.425 StartY=31.913 StartZ=0 EndX=0 EndY=0 EndZ=0
  constraints (14):
    c: Equal(g3,g2)
    c: Equal(g2,g0)
    c: Equal(g0,g1)
    c: Symmetric(g0,g2,g-1)
    c: Symmetric(g1,g3,g-1)
    c: Distance(g2,g-1) = 36.85
    c: Distance(g3,g-1) = 36.85
    c: Diameter(g3) = 6.2
    c: Coincident(g4,g0)
    c: Coincident(g4,g-1)
    c: Coincident(g5,g1)
    c: Coincident(g5,g4)
    c: Angle(g4,g-1) = 0.523599
    c: Angle(g5,g-1) = 1.0472
FEATURE [PartDesign::Pocket] Pocket004
  BaseFeature = -> Pocket001
  Direction = (0,0,-1)
  Length = 5
  Length2 = 5
  Profile = -> Sketch013
  ReferenceAxis = -> Sketch013 [N_Axis]
  Refine = true
  Suppressed = false
  Type = 1
FEATURE [PartDesign::Body] Body006  label="testube_layer"
  AllowCompound = false
  Group = -> [Sketch008,Pad006,DatumPlane,Sketch009,Pocket,DatumLine,PolarPattern,Sketch010,Pocket001,Sketch013,Pocket004]
  Origin = -> Origin006
  Placement = pos=(0,0,-39) rot=(0,0,1;0rad)
  Tip = -> Pocket004
COMPONENT P97 — recipe-attached ("017_top_layer001", modeled in this document).
Construction recipe (the document's own serialized feature program — sketch geometry with constraints, then the solid features built on it; lengths are millimeters unless a unit is written):

FEATURE [Sketcher::SketchObject] Sketch021
  ArcFitTolerance = 1e-06
  AttachmentSupport = -> [XY_Plane012]
  FullyConstrained = true
  MakeInternals = false
  MapMode = 5
  expr: Constraints[1] = VarSet.tube_inner_dia
  expr: Constraints[40] = 12.3 mm + 0.5 mm
  sketch-geometry (18):
    g0: Circle CenterX=0 CenterY=0 CenterZ=0 NormalX=0 NormalY=0 NormalZ=1 AngleXU=0 Radius=42.45
    g1: LineSegment [constr] StartX=0 StartY=0 StartZ=0 EndX=17.475 EndY=30.2676 EndZ=0
    g2: LineSegment [constr] StartX=0 StartY=0 StartZ=0 EndX=17.475 EndY=-30.2676 EndZ=0
    g3: ArcOfCircle CenterX=0 CenterY=0 CenterZ=0 NormalX=0 NormalY=0 NormalZ=1 AngleXU=0 Radius=12.5 StartAngle=5.23599 EndAngle=7.33038
    g4: ArcOfCircle CenterX=0 CenterY=0 CenterZ=0 NormalX=0 NormalY=0 NormalZ=1 AngleXU=0 Radius=34.95 StartAngle=5.23599 EndAngle=7.33038
    g5: LineSegment StartX=6.25 StartY=-10.8253 StartZ=0 EndX=4.07179 EndY=-23.0526 EndZ=0
    g6: LineSegment StartX=17.475 StartY=-30.2676 StartZ=0 EndX=4.07179 EndY=-23.0526 EndZ=0
    g7: LineSegment StartX=17.475 StartY=30.2676 StartZ=0 EndX=4.0718 EndY=23.0526 EndZ=0
    g8: LineSegment StartX=4.0718 StartY=23.0526 StartZ=0 EndX=6.25 EndY=10.8253 EndZ=0
    g9: LineSegment [constr] StartX=11 StartY=-19.0526 StartZ=0 EndX=4.07179 EndY=-23.0526 EndZ=0
    g10: LineSegment [constr] StartX=11 StartY=19.0526 StartZ=0 EndX=4.0718 EndY=23.0526 EndZ=0
    g11: LineSegment StartX=-17.65 StartY=6.4 StartZ=0 EndX=-17.65 EndY=-6.4 EndZ=0
    g12: LineSegment StartX=-17.65 StartY=-6.4 StartZ=0 EndX=5.85 EndY=-6.4 EndZ=0
    g13: LineSegment StartX=5.85 StartY=-6.4 StartZ=0 EndX=5.85 EndY=6.4 EndZ=0
    g14: LineSegment StartX=5.85 StartY=6.4 StartZ=0 EndX=-17.65 EndY=6.4 EndZ=0
    g15: GeomPoint [constr] X=-5.9 Y=0 Z=0
    g16: Circle CenterX=8.25 CenterY=0 CenterZ=0 NormalX=0 NormalY=0 NormalZ=1 AngleXU=0 Radius=0.75
    g17: Circle CenterX=-20.05 CenterY=0 CenterZ=0 NormalX=0 NormalY=0 NormalZ=1 AngleXU=0 Radius=0.75
  constraints (49):
    c: Coincident(g0,g-1)
    c: Diameter(g0) = 84.9
    c: Coincident(g1,g0)
    c: Coincident(g2,g0)
    c: Distance(g2,g2) = 34.95
    c: Angle(g2,g1) = 2.0944
    c: Angle(g1,g-2) = 0.523599
    c: Coincident(g3,g0)
    c: PointOnObject(g3,g1)
    c: PointOnObject(g3,g2)
    c: Diameter(g3) = 25
    c: Coincident(g4,g0)
    c: Coincident(g4,g2)
    c: Coincident(g1,g4)
    c: Coincident(g5,g3)
    c: Coincident(g6,g2)
    c: Coincident(g6,g5)
    c: Coincident(g7,g1)
    c: Coincident(g8,g7)
    c: Coincident(g8,g3)
    c: PointOnObject(g9,g2)
    c: Coincident(g9,g5)
    c: Perpendicular(g2,g9)
    c: PointOnObject(g10,g1)
    c: Coincident(g10,g7)
    c: Distance(g9,g-1) = 22
    c: Distance(g9,g5) = 8
    c: Distance(g10,g7) = 8
    c: Perpendicular(g1,g10)
    c: Distance(g10,g-1) = 22
    c: Coincident(g11,g12)
    c: Coincident(g12,g13)
    c: Coincident(g13,g14)
    c: Coincident(g14,g11)
    c: Vertical(g11)
    c: Vertical(g13)
    c: Horizontal(g12)
    c: Horizontal(g14)
    c: Symmetric(g13,g11,g15)
    c: PointOnObject(g15,g-1)
    c: DistanceY(g11,g11) = 12.8
    c: DistanceX(g14,g14) = 23.5
    c: DistanceX(g15,g-1) = 5.9
    c: Diameter(g16) = 1.5
    c: PointOnObject(g16,g-1)
    c: Diameter(g17) = 1.5
    c: PointOnObject(g17,g-1)
    c: Distance(g17,g11) = 2.4
    c: Distance(g16,g13) = 2.4
FEATURE [PartDesign::Pad] Pad010
  Direction = (0,0,1)
  Length = 17.5
  Length2 = 10
  Profile = -> Sketch021
  ReferenceAxis = -> Sketch021 [N_Axis]
  Refine = true
  Suppressed = false
  Type = 0
  expr: Length = VarSet.mdf_thick
FEATURE [PartDesign::Plane] DatumPlane005
  AttachmentOffset = pos=(0,0,42.45) rot=(0,0,1;0rad)
  AttachmentSupport = -> [YZ_Plane012]
  Length = 97.8895
  MapMode = 5
  Placement = pos=(42.45,0,0) rot=(0.57735,0.57735,0.57735;2.0944rad)
  ResizeMode = 0
  Width = 63.0278
  expr: .AttachmentOffset.Base.z = VarSet.tube_inner_dia / 2
FEATURE [Sketcher::SketchObject] Sketch025
  ArcFitTolerance = 1e-06
  AttachmentSupport = -> [DatumPlane005]
  FullyConstrained = true
  MakeInternals = false
  MapMode = 5
  Placement = pos=(42.45,0,0) rot=(0.57735,0.57735,0.57735;2.0944rad)
  expr: Constraints[2] = VarSet.mdf_thick / 2
  sketch-geometry (1):
    g0: Circle CenterX=0 CenterY=8.75 CenterZ=0 NormalX=0 NormalY=0 NormalZ=1 AngleXU=0 Radius=1
  constraints (3):
    c: Diameter(g0) = 2
    c: PointOnObject(g0,g-2)
    c: Distance(g0,g-1) = 8.75
FEATURE [PartDesign::Pocket] Pocket013
  BaseFeature = -> Pad010
  Direction = (-1,0,0)
  Length = 5
  Length2 = 5
  Profile = -> Sketch025
  ReferenceAxis = -> Sketch025 [N_Axis]
  Refine = true
  Suppressed = false
  Type = 0
FEATURE [PartDesign::PolarPattern] PolarPattern002
  Angle = 180
  Axis = -> Z_Axis012
  BaseFeature = -> Pocket013
  Mode = 0
  Occurrences = 3
  Offset = 120
  Originals = -> [Pocket013]
  Refine = true
  Suppressed = false
  TransformMode = 0
FEATURE [PartDesign::Body] Body010  label="top_layer"
  AllowCompound = false
  Group = -> [Sketch021,Pad010,DatumPlane005,Sketch025,Pocket013,PolarPattern002]
  Origin = -> Origin012
  Tip = -> PolarPattern002
COMPONENT P98 — recipe-attached ("049_wire-brown001", modeled in this document).
Construction recipe (the document's own serialized feature program — sketch geometry with constraints, then the solid features built on it; lengths are millimeters unless a unit is written):

FEATURE [PartDesign::Plane] DatumPlane008
  AttachmentOffset = pos=(0,0,60) rot=(0,0,1;0rad)
  AttachmentSupport = -> [YZ_Plane028]
  Length = 63.084
  MapMode = 5
  Placement = pos=(60,0,0) rot=(0.57735,0.57735,0.57735;2.0944rad)
  ResizeMode = 0
  Width = 98.6796
FEATURE [Sketcher::SketchObject] Sketch031
  ArcFitTolerance = 1e-06
  AttachmentSupport = -> [XZ_Plane028]
  FullyConstrained = true
  MakeInternals = false
  MapMode = 5
  Placement = pos=(0,0,0) rot=(1,0,0;1.5708rad)
  sketch-geometry (7):
    g0-g3: Circle [constr] x4 (B-spline internal-alignment scaffolding for g4; pole/knot coordinates omitted)
    g4: BSplineCurve PolesCount=4 KnotsCount=2 Degree=3 IsPeriodic=0
    g5: GeomPoint [constr] X=0 Y=60 Z=0
    g6: GeomPoint [constr] X=60 Y=0 Z=0
  constraints (14):
    c: Weight(g0) = 1
    c: Equal(g0,g1)
    c: Equal(g0,g2)
    c: Equal(g0,g3)
    c: InternalAlignment(g0-g3 -> g4) x4
    c: InternalAlignment(g5,g4)
    c: InternalAlignment(g6,g4)
    c: PointOnObject(g0,g-2)
    c: PointOnObject(g2,g-1)
    c: DistanceX(g-1,g4) = 60
    c: Symmetric(g-1,g4,g2)
    c: Vertical(g1,g2)
    c: DistanceY(g-1,g4) = 60
    c: Horizontal(g1,g4)
FEATURE [Sketcher::SketchObject] Sketch032
  ArcFitTolerance = 1e-06
  AttachmentSupport = -> [DatumPlane008]
  FullyConstrained = true
  MakeInternals = false
  MapMode = 5
  Placement = pos=(60,0,0) rot=(0.57735,0.57735,0.57735;2.0944rad)
  sketch-geometry (1):
    g0: Circle CenterX=0 CenterY=0 CenterZ=0 NormalX=0 NormalY=0 NormalZ=1 AngleXU=0 Radius=0.6
  constraints (2):
    c: Coincident(g0,g-1)
    c: Diameter(g0) = 1.2
FEATURE [PartDesign::AdditivePipe] AdditivePipe001
  AuxilleryCurvelinear = true
  AuxillerySpineTangent = false
  Binormal = (0,0,0)
  Mode = 0
  Placement = pos=(60,0,0) rot=(0.57735,0.57735,0.57735;2.0944rad)
  Profile = -> Sketch032
  Refine = true
  Spine = -> Sketch031 [Edge1]
  SpineTangent = false
  Suppressed = false
  Transformation = 0
  Transition = 0
FEATURE [PartDesign::Body] Body017  label="wire-brown"
  AllowCompound = false
  Group = -> [Sketch031,DatumPlane008,Sketch032,AdditivePipe001]
  Origin = -> Origin028
  Tip = -> AdditivePipe001
COMPONENT P99 — same part as P98; its construction recipe is shown at P98.
COMPONENT P100 — recipe-attached ("047_wire-orange001", modeled in this document).
Construction recipe (the document's own serialized feature program — sketch geometry with constraints, then the solid features built on it; lengths are millimeters unless a unit is written):

FEATURE [PartDesign::Plane] DatumPlane009
  AttachmentOffset = pos=(0,0,60) rot=(0,0,1;0rad)
  AttachmentSupport = -> [YZ_Plane029]
  Length = 63.084
  MapMode = 5
  Placement = pos=(60,0,0) rot=(0.57735,0.57735,0.57735;2.0944rad)
  ResizeMode = 0
  Width = 98.6796
FEATURE [Sketcher::SketchObject] Sketch033
  ArcFitTolerance = 1e-06
  AttachmentSupport = -> [XZ_Plane029]
  FullyConstrained = true
  MakeInternals = false
  MapMode = 5
  Placement = pos=(0,0,0) rot=(1,0,0;1.5708rad)
  sketch-geometry (7):
    g0-g3: Circle [constr] x4 (B-spline internal-alignment scaffolding for g4; pole/knot coordinates omitted)
    g4: BSplineCurve PolesCount=4 KnotsCount=2 Degree=3 IsPeriodic=0
    g5: GeomPoint [constr] X=0 Y=60 Z=0
    g6: GeomPoint [constr] X=60 Y=0 Z=0
  constraints (14):
    c: Weight(g0) = 1
    c: Equal(g0,g1)
    c: Equal(g0,g2)
    c: Equal(g0,g3)
    c: InternalAlignment(g0-g3 -> g4) x4
    c: InternalAlignment(g5,g4)
    c: InternalAlignment(g6,g4)
    c: PointOnObject(g0,g-2)
    c: PointOnObject(g2,g-1)
    c: DistanceX(g-1,g4) = 60
    c: Symmetric(g-1,g4,g2)
    c: Vertical(g1,g2)
    c: DistanceY(g-1,g4) = 60
    c: Horizontal(g1,g4)
FEATURE [Sketcher::SketchObject] Sketch034
  ArcFitTolerance = 1e-06
  AttachmentSupport = -> [DatumPlane009]
  FullyConstrained = true
  MakeInternals = false
  MapMode = 5
  Placement = pos=(60,0,0) rot=(0.57735,0.57735,0.57735;2.0944rad)
  sketch-geometry (1):
    g0: Circle CenterX=0 CenterY=0 CenterZ=0 NormalX=0 NormalY=0 NormalZ=1 AngleXU=0 Radius=0.6
  constraints (2):
    c: Coincident(g0,g-1)
    c: Diameter(g0) = 1.2
FEATURE [PartDesign::AdditivePipe] AdditivePipe002
  AuxilleryCurvelinear = true
  AuxillerySpineTangent = false
  Binormal = (0,0,0)
  Mode = 0
  Placement = pos=(60,0,0) rot=(0.57735,0.57735,0.57735;2.0944rad)
  Profile = -> Sketch034
  Refine = true
  Spine = -> Sketch033 [Edge1]
  SpineTangent = false
  Suppressed = false
  Transformation = 0
  Transition = 0
FEATURE [PartDesign::Body] Body018  label="wire-orange"
  AllowCompound = false
  Group = -> [Sketch033,DatumPlane009,Sketch034,AdditivePipe002]
  Origin = -> Origin029
  Placement = pos=(0,14,0) rot=(0,0,1;0rad)
  Tip = -> AdditivePipe002
COMPONENT P101 — same part as P100; its construction recipe is shown at P100.
COMPONENT P102 — recipe-attached ("048_wire-red001", modeled in this document).
Construction recipe (the document's own serialized feature program — sketch geometry with constraints, then the solid features built on it; lengths are millimeters unless a unit is written):

FEATURE [Sketcher::SketchObject] Sketch029
  ArcFitTolerance = 1e-06
  AttachmentSupport = -> [XZ_Plane027]
  FullyConstrained = true
  MakeInternals = false
  MapMode = 5
  Placement = pos=(0,0,0) rot=(1,0,0;1.5708rad)
  sketch-geometry (7):
    g0-g3: Circle [constr] x4 (B-spline internal-alignment scaffolding for g4; pole/knot coordinates omitted)
    g4: BSplineCurve PolesCount=4 KnotsCount=2 Degree=3 IsPeriodic=0
    g5: GeomPoint [constr] X=0 Y=60 Z=0
    g6: GeomPoint [constr] X=60 Y=0 Z=0
  constraints (14):
    c: Weight(g0) = 1
    c: Equal(g0,g1)
    c: Equal(g0,g2)
    c: Equal(g0,g3)
    c: InternalAlignment(g0-g3 -> g4) x4
    c: InternalAlignment(g5,g4)
    c: InternalAlignment(g6,g4)
    c: PointOnObject(g0,g-2)
    c: PointOnObject(g2,g-1)
    c: DistanceX(g-1,g4) = 60
    c: Symmetric(g-1,g4,g2)
    c: Vertical(g1,g2)
    c: DistanceY(g-1,g4) = 60
    c: Horizontal(g1,g4)
FEATURE [PartDesign::Plane] DatumPlane007
  AttachmentOffset = pos=(0,0,60) rot=(0,0,1;0rad)
  AttachmentSupport = -> [YZ_Plane027]
  Length = 63.084
  MapMode = 5
  Placement = pos=(60,0,0) rot=(0.57735,0.57735,0.57735;2.0944rad)
  ResizeMode = 0
  Width = 98.6796
FEATURE [Sketcher::SketchObject] Sketch030
  ArcFitTolerance = 1e-06
  AttachmentSupport = -> [DatumPlane007]
  FullyConstrained = true
  MakeInternals = false
  MapMode = 5
  Placement = pos=(60,0,0) rot=(0.57735,0.57735,0.57735;2.0944rad)
  sketch-geometry (1):
    g0: Circle CenterX=0 CenterY=0 CenterZ=0 NormalX=0 NormalY=0 NormalZ=1 AngleXU=0 Radius=0.6
  constraints (2):
    c: Coincident(g0,g-1)
    c: Diameter(g0) = 1.2
FEATURE [PartDesign::AdditivePipe] AdditivePipe
  AuxilleryCurvelinear = true
  AuxillerySpineTangent = false
  Binormal = (0,0,0)
  Mode = 0
  Placement = pos=(60,0,0) rot=(0.57735,0.57735,0.57735;2.0944rad)
  Profile = -> Sketch030
  Refine = true
  Spine = -> Sketch029 [Edge1]
  SpineTangent = false
  Suppressed = false
  Transformation = 0
  Transition = 0
FEATURE [PartDesign::Body] Body016  label="wire-red"
  AllowCompound = false
  Group = -> [Sketch029,DatumPlane007,Sketch030,AdditivePipe]
  Origin = -> Origin027
  Placement = pos=(0,-14,0) rot=(0,0,1;0rad)
  Tip = -> AdditivePipe
COMPONENT P103 — same part as P102; its construction recipe is shown at P102.
PROVENANCE & LICENSES
A FreeCAD (.FCStd) document from a public repository crawl; recipes are the document's own serialized feature recipes (and, for linked parts, companion documents' recipes).
License: as declared in the source repository (recorded in the dataset sidecar).
